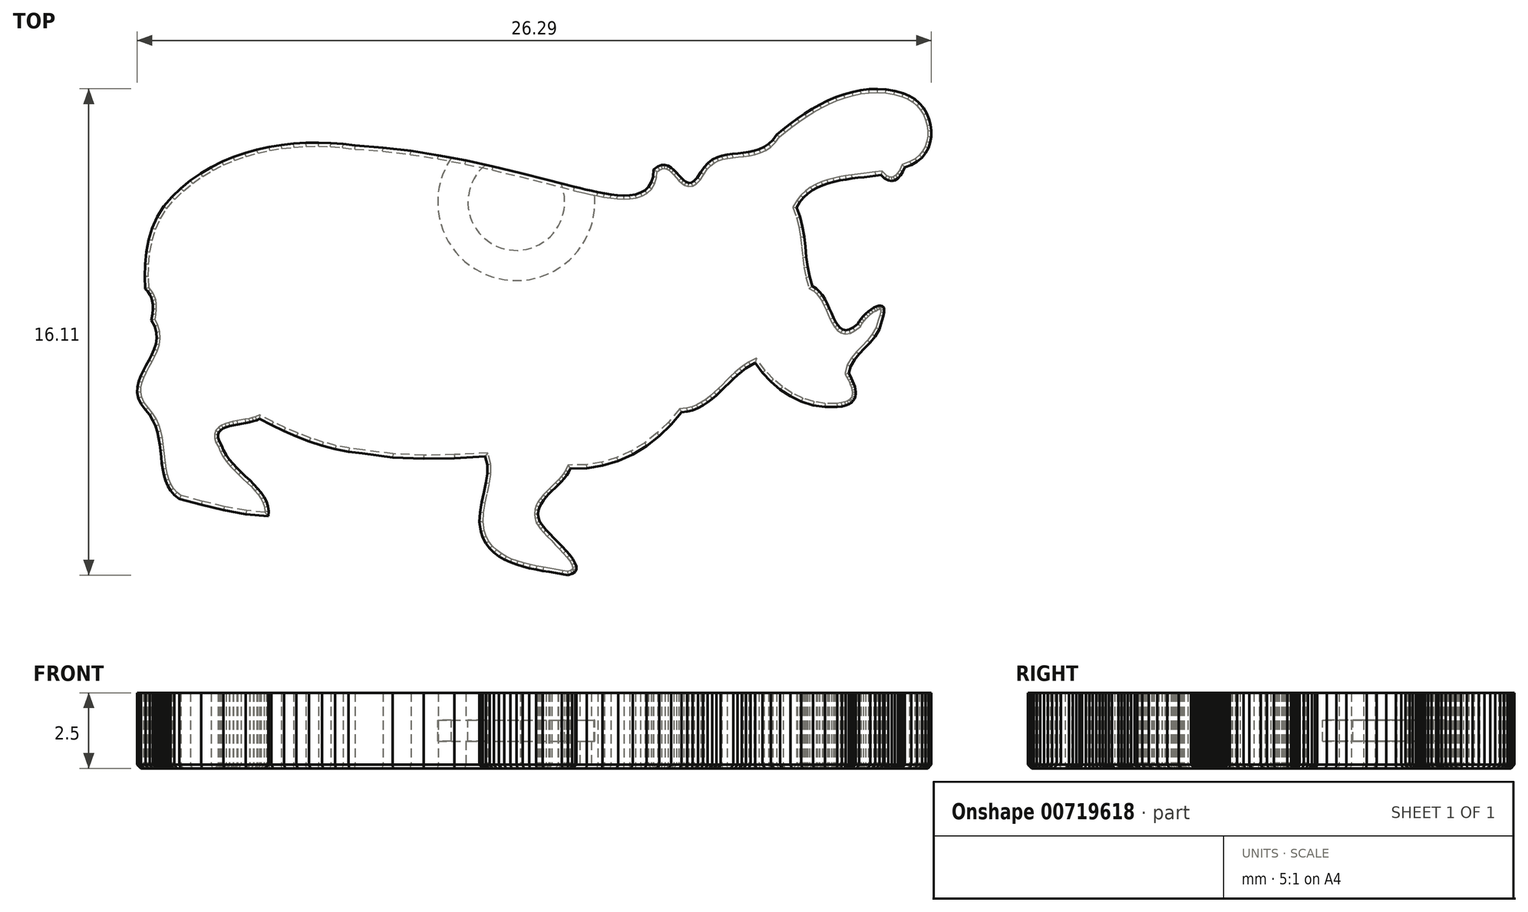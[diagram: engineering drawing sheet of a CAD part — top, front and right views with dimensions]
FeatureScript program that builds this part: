
annotation { "Feature Type Name" : "Feature", "Feature Type Description" : "" }
export const myFeature = defineFeature(function(context is Context, id is Id, definition is map)
    precondition{}
    {
        {
            var Q0;
            Q0=qCreatedBy(makeId("Top.planeOp"),FACE);
            var sketch = newSketch(context, id + "F0", { "sketchPlane" : qUnion([Q0])});
            skLineSegment(sketch, "E0", {"start": v(0.97, -8.24) * mm, "end": v(0.77, -8.2) * mm});
            skLineSegment(sketch, "E1", {"start": v(0.77, -8.2) * mm, "end": v(0.56, -8.17) * mm});
            skLineSegment(sketch, "E2", {"start": v(0.56, -8.17) * mm, "end": v(0.35, -8.14) * mm});
            skLineSegment(sketch, "E3", {"start": v(0.35, -8.14) * mm, "end": v(0.13, -8.1) * mm});
            skLineSegment(sketch, "E4", {"start": v(0.13, -8.1) * mm, "end": v(-0.09, -8.06) * mm});
            skLineSegment(sketch, "E5", {"start": v(-0.09, -8.06) * mm, "end": v(-0.3, -8.01) * mm});
            skLineSegment(sketch, "E6", {"start": v(-0.3, -8.01) * mm, "end": v(-0.52, -7.96) * mm});
            skLineSegment(sketch, "E7", {"start": v(-0.52, -7.96) * mm, "end": v(-0.73, -7.9) * mm});
            skLineSegment(sketch, "E8", {"start": v(-0.73, -7.9) * mm, "end": v(-0.94, -7.82) * mm});
            skLineSegment(sketch, "E9", {"start": v(-0.94, -7.82) * mm, "end": v(-1.13, -7.73) * mm});
            skLineSegment(sketch, "E10", {"start": v(-1.13, -7.73) * mm, "end": v(-1.3, -7.62) * mm});
            skLineSegment(sketch, "E11", {"start": v(-1.3, -7.62) * mm, "end": v(-1.47, -7.5) * mm});
            skLineSegment(sketch, "E12", {"start": v(-1.47, -7.5) * mm, "end": v(-1.62, -7.36) * mm});
            skLineSegment(sketch, "E13", {"start": v(-1.62, -7.36) * mm, "end": v(-1.74, -7.2) * mm});
            skLineSegment(sketch, "E14", {"start": v(-1.74, -7.2) * mm, "end": v(-1.84, -7) * mm});
            skLineSegment(sketch, "E15", {"start": v(-1.84, -7) * mm, "end": v(-1.92, -6.8) * mm});
            skLineSegment(sketch, "E16", {"start": v(-1.92, -6.8) * mm, "end": v(-1.96, -6.48) * mm});
            skLineSegment(sketch, "E17", {"start": v(-1.96, -6.48) * mm, "end": v(-1.94, -6.16) * mm});
            skLineSegment(sketch, "E18", {"start": v(-1.94, -6.16) * mm, "end": v(-1.89, -5.83) * mm});
            skLineSegment(sketch, "E19", {"start": v(-1.89, -5.83) * mm, "end": v(-1.81, -5.5) * mm});
            skLineSegment(sketch, "E20", {"start": v(-1.81, -5.5) * mm, "end": v(-1.74, -5.18) * mm});
            skLineSegment(sketch, "E21", {"start": v(-1.74, -5.18) * mm, "end": v(-1.7, -4.88) * mm});
            skLineSegment(sketch, "E22", {"start": v(-1.7, -4.88) * mm, "end": v(-1.7, -4.58) * mm});
            skLineSegment(sketch, "E23", {"start": v(-1.7, -4.58) * mm, "end": v(-1.77, -4.31) * mm});
            skLineSegment(sketch, "E24", {"start": v(-1.77, -4.31) * mm, "end": v(-2.79, -4.37) * mm});
            skLineSegment(sketch, "E25", {"start": v(-2.79, -4.37) * mm, "end": v(-3.8, -4.39) * mm});
            skLineSegment(sketch, "E26", {"start": v(-3.8, -4.39) * mm, "end": v(-4.83, -4.34) * mm});
            skLineSegment(sketch, "E27", {"start": v(-4.83, -4.34) * mm, "end": v(-5.84, -4.2) * mm});
            skLineSegment(sketch, "E28", {"start": v(-5.84, -4.2) * mm, "end": v(-6.3, -4.15) * mm});
            skLineSegment(sketch, "E29", {"start": v(-6.3, -4.15) * mm, "end": v(-6.73, -4.06) * mm});
            skLineSegment(sketch, "E30", {"start": v(-6.73, -4.06) * mm, "end": v(-7.17, -3.95) * mm});
            skLineSegment(sketch, "E31", {"start": v(-7.17, -3.95) * mm, "end": v(-7.6, -3.8) * mm});
            skLineSegment(sketch, "E32", {"start": v(-7.6, -3.8) * mm, "end": v(-8.02, -3.64) * mm});
            skLineSegment(sketch, "E33", {"start": v(-8.02, -3.64) * mm, "end": v(-8.43, -3.46) * mm});
            skLineSegment(sketch, "E34", {"start": v(-8.43, -3.46) * mm, "end": v(-8.84, -3.27) * mm});
            skLineSegment(sketch, "E35", {"start": v(-8.84, -3.27) * mm, "end": v(-9.24, -3.07) * mm});
            skLineSegment(sketch, "E36", {"start": v(-9.24, -3.07) * mm, "end": v(-9.33, -3.1) * mm});
            skLineSegment(sketch, "E37", {"start": v(-9.33, -3.1) * mm, "end": v(-9.44, -3.14) * mm});
            skLineSegment(sketch, "E38", {"start": v(-9.44, -3.14) * mm, "end": v(-9.56, -3.17) * mm});
            skLineSegment(sketch, "E39", {"start": v(-9.56, -3.17) * mm, "end": v(-9.7, -3.2) * mm});
            skLineSegment(sketch, "E40", {"start": v(-9.7, -3.2) * mm, "end": v(-9.83, -3.22) * mm});
            skLineSegment(sketch, "E41", {"start": v(-9.83, -3.22) * mm, "end": v(-9.97, -3.25) * mm});
            skLineSegment(sketch, "E42", {"start": v(-9.97, -3.25) * mm, "end": v(-10.1, -3.27) * mm});
            skLineSegment(sketch, "E43", {"start": v(-10.1, -3.27) * mm, "end": v(-10.23, -3.3) * mm});
            skLineSegment(sketch, "E44", {"start": v(-10.23, -3.3) * mm, "end": v(-10.34, -3.34) * mm});
            skLineSegment(sketch, "E45", {"start": v(-10.34, -3.34) * mm, "end": v(-10.44, -3.39) * mm});
            skLineSegment(sketch, "E46", {"start": v(-10.44, -3.39) * mm, "end": v(-10.52, -3.44) * mm});
            skLineSegment(sketch, "E47", {"start": v(-10.52, -3.44) * mm, "end": v(-10.58, -3.5) * mm});
            skLineSegment(sketch, "E48", {"start": v(-10.58, -3.5) * mm, "end": v(-10.6, -3.59) * mm});
            skLineSegment(sketch, "E49", {"start": v(-10.6, -3.59) * mm, "end": v(-10.6, -3.69) * mm});
            skLineSegment(sketch, "E50", {"start": v(-10.6, -3.69) * mm, "end": v(-10.57, -3.8) * mm});
            skLineSegment(sketch, "E51", {"start": v(-10.57, -3.8) * mm, "end": v(-10.5, -3.94) * mm});
            skLineSegment(sketch, "E52", {"start": v(-10.5, -3.94) * mm, "end": v(-10.43, -4.1) * mm});
            skLineSegment(sketch, "E53", {"start": v(-10.43, -4.1) * mm, "end": v(-10.34, -4.26) * mm});
            skLineSegment(sketch, "E54", {"start": v(-10.34, -4.26) * mm, "end": v(-10.24, -4.4) * mm});
            skLineSegment(sketch, "E55", {"start": v(-10.24, -4.4) * mm, "end": v(-10.12, -4.55) * mm});
            skLineSegment(sketch, "E56", {"start": v(-10.12, -4.55) * mm, "end": v(-9.98, -4.7) * mm});
            skLineSegment(sketch, "E57", {"start": v(-9.98, -4.7) * mm, "end": v(-9.84, -4.83) * mm});
            skLineSegment(sketch, "E58", {"start": v(-9.84, -4.83) * mm, "end": v(-9.7, -4.96) * mm});
            skLineSegment(sketch, "E59", {"start": v(-9.7, -4.96) * mm, "end": v(-9.56, -5.1) * mm});
            skLineSegment(sketch, "E60", {"start": v(-9.56, -5.1) * mm, "end": v(-9.43, -5.23) * mm});
            skLineSegment(sketch, "E61", {"start": v(-9.43, -5.23) * mm, "end": v(-9.3, -5.37) * mm});
            skLineSegment(sketch, "E62", {"start": v(-9.3, -5.37) * mm, "end": v(-9.18, -5.5) * mm});
            skLineSegment(sketch, "E63", {"start": v(-9.18, -5.5) * mm, "end": v(-9.09, -5.65) * mm});
            skLineSegment(sketch, "E64", {"start": v(-9.09, -5.65) * mm, "end": v(-9, -5.8) * mm});
            skLineSegment(sketch, "E65", {"start": v(-9, -5.8) * mm, "end": v(-8.96, -5.95) * mm});
            skLineSegment(sketch, "E66", {"start": v(-8.96, -5.95) * mm, "end": v(-8.94, -6.12) * mm});
            skLineSegment(sketch, "E67", {"start": v(-8.94, -6.12) * mm, "end": v(-8.95, -6.3) * mm});
            skLineSegment(sketch, "E68", {"start": v(-8.95, -6.3) * mm, "end": v(-9.7, -6.22) * mm});
            skLineSegment(sketch, "E69", {"start": v(-9.7, -6.22) * mm, "end": v(-10.43, -6.08) * mm});
            skLineSegment(sketch, "E70", {"start": v(-10.43, -6.08) * mm, "end": v(-11.17, -5.9) * mm});
            skLineSegment(sketch, "E71", {"start": v(-11.17, -5.9) * mm, "end": v(-11.9, -5.71) * mm});
            skLineSegment(sketch, "E72", {"start": v(-11.9, -5.71) * mm, "end": v(-12.05, -5.58) * mm});
            skLineSegment(sketch, "E73", {"start": v(-12.05, -5.58) * mm, "end": v(-12.18, -5.44) * mm});
            skLineSegment(sketch, "E74", {"start": v(-12.18, -5.44) * mm, "end": v(-12.28, -5.28) * mm});
            skLineSegment(sketch, "E75", {"start": v(-12.28, -5.28) * mm, "end": v(-12.35, -5.11) * mm});
            skLineSegment(sketch, "E76", {"start": v(-12.35, -5.11) * mm, "end": v(-12.4, -4.93) * mm});
            skLineSegment(sketch, "E77", {"start": v(-12.4, -4.93) * mm, "end": v(-12.44, -4.73) * mm});
            skLineSegment(sketch, "E78", {"start": v(-12.44, -4.73) * mm, "end": v(-12.47, -4.53) * mm});
            skLineSegment(sketch, "E79", {"start": v(-12.47, -4.53) * mm, "end": v(-12.5, -4.33) * mm});
            skLineSegment(sketch, "E80", {"start": v(-12.5, -4.33) * mm, "end": v(-12.52, -4.12) * mm});
            skLineSegment(sketch, "E81", {"start": v(-12.52, -4.12) * mm, "end": v(-12.54, -3.91) * mm});
            skLineSegment(sketch, "E82", {"start": v(-12.54, -3.91) * mm, "end": v(-12.57, -3.7) * mm});
            skLineSegment(sketch, "E83", {"start": v(-12.57, -3.7) * mm, "end": v(-12.62, -3.5) * mm});
            skLineSegment(sketch, "E84", {"start": v(-12.62, -3.5) * mm, "end": v(-12.68, -3.3) * mm});
            skLineSegment(sketch, "E85", {"start": v(-12.68, -3.3) * mm, "end": v(-12.76, -3.12) * mm});
            skLineSegment(sketch, "E86", {"start": v(-12.76, -3.12) * mm, "end": v(-12.87, -2.94) * mm});
            skLineSegment(sketch, "E87", {"start": v(-12.87, -2.94) * mm, "end": v(-13.01, -2.77) * mm});
            skLineSegment(sketch, "E88", {"start": v(-13.01, -2.77) * mm, "end": v(-13.16, -2.57) * mm});
            skLineSegment(sketch, "E89", {"start": v(-13.16, -2.57) * mm, "end": v(-13.25, -2.38) * mm});
            skLineSegment(sketch, "E90", {"start": v(-13.25, -2.38) * mm, "end": v(-13.29, -2.19) * mm});
            skLineSegment(sketch, "E91", {"start": v(-13.29, -2.19) * mm, "end": v(-13.28, -2) * mm});
            skLineSegment(sketch, "E92", {"start": v(-13.28, -2) * mm, "end": v(-13.24, -1.82) * mm});
            skLineSegment(sketch, "E93", {"start": v(-13.24, -1.82) * mm, "end": v(-13.18, -1.65) * mm});
            skLineSegment(sketch, "E94", {"start": v(-13.18, -1.65) * mm, "end": v(-13.1, -1.47) * mm});
            skLineSegment(sketch, "E95", {"start": v(-13.1, -1.47) * mm, "end": v(-13, -1.3) * mm});
            skLineSegment(sketch, "E96", {"start": v(-13, -1.3) * mm, "end": v(-12.9, -1.12) * mm});
            skLineSegment(sketch, "E97", {"start": v(-12.9, -1.12) * mm, "end": v(-12.8, -0.94) * mm});
            skLineSegment(sketch, "E98", {"start": v(-12.8, -0.94) * mm, "end": v(-12.73, -0.76) * mm});
            skLineSegment(sketch, "E99", {"start": v(-12.73, -0.76) * mm, "end": v(-12.67, -0.58) * mm});
            skLineSegment(sketch, "E100", {"start": v(-12.67, -0.58) * mm, "end": v(-12.65, -0.4) * mm});
            skLineSegment(sketch, "E101", {"start": v(-12.65, -0.4) * mm, "end": v(-12.66, -0.2) * mm});
            skLineSegment(sketch, "E102", {"start": v(-12.66, -0.2) * mm, "end": v(-12.71, 0) * mm});
            skLineSegment(sketch, "E103", {"start": v(-12.71, 0) * mm, "end": v(-12.82, 0.2) * mm});
            skLineSegment(sketch, "E104", {"start": v(-12.82, 0.2) * mm, "end": v(-12.79, 0.4) * mm});
            skLineSegment(sketch, "E105", {"start": v(-12.79, 0.4) * mm, "end": v(-12.77, 0.58) * mm});
            skLineSegment(sketch, "E106", {"start": v(-12.77, 0.58) * mm, "end": v(-12.77, 0.72) * mm});
            skLineSegment(sketch, "E107", {"start": v(-12.77, 0.72) * mm, "end": v(-12.79, 0.85) * mm});
            skLineSegment(sketch, "E108", {"start": v(-12.79, 0.85) * mm, "end": v(-12.82, 0.96) * mm});
            skLineSegment(sketch, "E109", {"start": v(-12.82, 0.96) * mm, "end": v(-12.87, 1.06) * mm});
            skLineSegment(sketch, "E110", {"start": v(-12.87, 1.06) * mm, "end": v(-12.94, 1.15) * mm});
            skLineSegment(sketch, "E111", {"start": v(-12.94, 1.15) * mm, "end": v(-13.02, 1.24) * mm});
            skLineSegment(sketch, "E112", {"start": v(-13.02, 1.24) * mm, "end": v(-13.04, 1.65) * mm});
            skLineSegment(sketch, "E113", {"start": v(-13.04, 1.65) * mm, "end": v(-13.03, 2.06) * mm});
            skLineSegment(sketch, "E114", {"start": v(-13.03, 2.06) * mm, "end": v(-12.99, 2.47) * mm});
            skLineSegment(sketch, "E115", {"start": v(-12.99, 2.47) * mm, "end": v(-12.9, 2.87) * mm});
            skLineSegment(sketch, "E116", {"start": v(-12.9, 2.87) * mm, "end": v(-12.8, 3.25) * mm});
            skLineSegment(sketch, "E117", {"start": v(-12.8, 3.25) * mm, "end": v(-12.63, 3.62) * mm});
            skLineSegment(sketch, "E118", {"start": v(-12.63, 3.62) * mm, "end": v(-12.4, 3.97) * mm});
            skLineSegment(sketch, "E119", {"start": v(-12.4, 3.97) * mm, "end": v(-12.14, 4.29) * mm});
            skLineSegment(sketch, "E120", {"start": v(-12.14, 4.29) * mm, "end": v(-11.84, 4.58) * mm});
            skLineSegment(sketch, "E121", {"start": v(-11.84, 4.58) * mm, "end": v(-11.52, 4.83) * mm});
            skLineSegment(sketch, "E122", {"start": v(-11.52, 4.83) * mm, "end": v(-11.19, 5.07) * mm});
            skLineSegment(sketch, "E123", {"start": v(-11.19, 5.07) * mm, "end": v(-10.84, 5.27) * mm});
            skLineSegment(sketch, "E124", {"start": v(-10.84, 5.27) * mm, "end": v(-10.48, 5.45) * mm});
            skLineSegment(sketch, "E125", {"start": v(-10.48, 5.45) * mm, "end": v(-10.1, 5.61) * mm});
            skLineSegment(sketch, "E126", {"start": v(-10.1, 5.61) * mm, "end": v(-9.72, 5.74) * mm});
            skLineSegment(sketch, "E127", {"start": v(-9.72, 5.74) * mm, "end": v(-9.32, 5.85) * mm});
            skLineSegment(sketch, "E128", {"start": v(-9.32, 5.85) * mm, "end": v(-8.92, 5.94) * mm});
            skLineSegment(sketch, "E129", {"start": v(-8.92, 5.94) * mm, "end": v(-8.52, 6) * mm});
            skLineSegment(sketch, "E130", {"start": v(-8.52, 6) * mm, "end": v(-8.1, 6.05) * mm});
            skLineSegment(sketch, "E131", {"start": v(-8.1, 6.05) * mm, "end": v(-7.7, 6.08) * mm});
            skLineSegment(sketch, "E132", {"start": v(-7.7, 6.08) * mm, "end": v(-7.29, 6.08) * mm});
            skLineSegment(sketch, "E133", {"start": v(-7.29, 6.08) * mm, "end": v(-6.88, 6.07) * mm});
            skLineSegment(sketch, "E134", {"start": v(-6.88, 6.07) * mm, "end": v(-6.47, 6.04) * mm});
            skLineSegment(sketch, "E135", {"start": v(-6.47, 6.04) * mm, "end": v(-6.07, 6) * mm});
            skLineSegment(sketch, "E136", {"start": v(-6.07, 6) * mm, "end": v(-5.15, 5.92) * mm});
            skLineSegment(sketch, "E137", {"start": v(-5.15, 5.92) * mm, "end": v(-4.23, 5.81) * mm});
            skLineSegment(sketch, "E138", {"start": v(-4.23, 5.81) * mm, "end": v(-3.31, 5.67) * mm});
            skLineSegment(sketch, "E139", {"start": v(-3.31, 5.67) * mm, "end": v(-2.4, 5.5) * mm});
            skLineSegment(sketch, "E140", {"start": v(-2.4, 5.5) * mm, "end": v(-1.5, 5.3) * mm});
            skLineSegment(sketch, "E141", {"start": v(-1.5, 5.3) * mm, "end": v(-0.6, 5.08) * mm});
            skLineSegment(sketch, "E142", {"start": v(-0.6, 5.08) * mm, "end": v(0.3, 4.85) * mm});
            skLineSegment(sketch, "E143", {"start": v(0.3, 4.85) * mm, "end": v(1.2, 4.62) * mm});
            skLineSegment(sketch, "E144", {"start": v(1.2, 4.62) * mm, "end": v(1.36, 4.58) * mm});
            skLineSegment(sketch, "E145", {"start": v(1.36, 4.58) * mm, "end": v(1.55, 4.53) * mm});
            skLineSegment(sketch, "E146", {"start": v(1.55, 4.53) * mm, "end": v(1.75, 4.49) * mm});
            skLineSegment(sketch, "E147", {"start": v(1.75, 4.49) * mm, "end": v(1.96, 4.44) * mm});
            skLineSegment(sketch, "E148", {"start": v(1.96, 4.44) * mm, "end": v(2.18, 4.4) * mm});
            skLineSegment(sketch, "E149", {"start": v(2.18, 4.4) * mm, "end": v(2.4, 4.37) * mm});
            skLineSegment(sketch, "E150", {"start": v(2.4, 4.37) * mm, "end": v(2.61, 4.34) * mm});
            skLineSegment(sketch, "E151", {"start": v(2.61, 4.34) * mm, "end": v(2.82, 4.33) * mm});
            skLineSegment(sketch, "E152", {"start": v(2.82, 4.33) * mm, "end": v(3.02, 4.34) * mm});
            skLineSegment(sketch, "E153", {"start": v(3.02, 4.34) * mm, "end": v(3.2, 4.37) * mm});
            skLineSegment(sketch, "E154", {"start": v(3.2, 4.37) * mm, "end": v(3.38, 4.42) * mm});
            skLineSegment(sketch, "E155", {"start": v(3.38, 4.42) * mm, "end": v(3.52, 4.5) * mm});
            skLineSegment(sketch, "E156", {"start": v(3.52, 4.5) * mm, "end": v(3.64, 4.62) * mm});
            skLineSegment(sketch, "E157", {"start": v(3.64, 4.62) * mm, "end": v(3.73, 4.77) * mm});
            skLineSegment(sketch, "E158", {"start": v(3.73, 4.77) * mm, "end": v(3.79, 4.96) * mm});
            skLineSegment(sketch, "E159", {"start": v(3.79, 4.96) * mm, "end": v(3.8, 5.19) * mm});
            skLineSegment(sketch, "E160", {"start": v(3.8, 5.19) * mm, "end": v(3.94, 5.29) * mm});
            skLineSegment(sketch, "E161", {"start": v(3.94, 5.29) * mm, "end": v(4.07, 5.34) * mm});
            skLineSegment(sketch, "E162", {"start": v(4.07, 5.34) * mm, "end": v(4.19, 5.35) * mm});
            skLineSegment(sketch, "E163", {"start": v(4.19, 5.35) * mm, "end": v(4.3, 5.32) * mm});
            skLineSegment(sketch, "E164", {"start": v(4.3, 5.32) * mm, "end": v(4.4, 5.26) * mm});
            skLineSegment(sketch, "E165", {"start": v(4.4, 5.26) * mm, "end": v(4.48, 5.18) * mm});
            skLineSegment(sketch, "E166", {"start": v(4.48, 5.18) * mm, "end": v(4.57, 5.1) * mm});
            skLineSegment(sketch, "E167", {"start": v(4.57, 5.1) * mm, "end": v(4.65, 5) * mm});
            skLineSegment(sketch, "E168", {"start": v(4.65, 5) * mm, "end": v(4.73, 4.91) * mm});
            skLineSegment(sketch, "E169", {"start": v(4.73, 4.91) * mm, "end": v(4.8, 4.84) * mm});
            skLineSegment(sketch, "E170", {"start": v(4.8, 4.84) * mm, "end": v(4.89, 4.78) * mm});
            skLineSegment(sketch, "E171", {"start": v(4.89, 4.78) * mm, "end": v(4.97, 4.75) * mm});
            skLineSegment(sketch, "E172", {"start": v(4.97, 4.75) * mm, "end": v(5.06, 4.76) * mm});
            skLineSegment(sketch, "E173", {"start": v(5.06, 4.76) * mm, "end": v(5.15, 4.82) * mm});
            skLineSegment(sketch, "E174", {"start": v(5.15, 4.82) * mm, "end": v(5.26, 4.93) * mm});
            skLineSegment(sketch, "E175", {"start": v(5.26, 4.93) * mm, "end": v(5.37, 5.1) * mm});
            skLineSegment(sketch, "E176", {"start": v(5.37, 5.1) * mm, "end": v(5.48, 5.28) * mm});
            skLineSegment(sketch, "E177", {"start": v(5.48, 5.28) * mm, "end": v(5.61, 5.41) * mm});
            skLineSegment(sketch, "E178", {"start": v(5.61, 5.41) * mm, "end": v(5.75, 5.52) * mm});
            skLineSegment(sketch, "E179", {"start": v(5.75, 5.52) * mm, "end": v(5.9, 5.6) * mm});
            skLineSegment(sketch, "E180", {"start": v(5.9, 5.6) * mm, "end": v(6.07, 5.65) * mm});
            skLineSegment(sketch, "E181", {"start": v(6.07, 5.65) * mm, "end": v(6.24, 5.68) * mm});
            skLineSegment(sketch, "E182", {"start": v(6.24, 5.68) * mm, "end": v(6.42, 5.7) * mm});
            skLineSegment(sketch, "E183", {"start": v(6.42, 5.7) * mm, "end": v(6.6, 5.73) * mm});
            skLineSegment(sketch, "E184", {"start": v(6.6, 5.73) * mm, "end": v(6.77, 5.75) * mm});
            skLineSegment(sketch, "E185", {"start": v(6.77, 5.75) * mm, "end": v(6.95, 5.77) * mm});
            skLineSegment(sketch, "E186", {"start": v(6.95, 5.77) * mm, "end": v(7.13, 5.8) * mm});
            skLineSegment(sketch, "E187", {"start": v(7.13, 5.8) * mm, "end": v(7.3, 5.86) * mm});
            skLineSegment(sketch, "E188", {"start": v(7.3, 5.86) * mm, "end": v(7.46, 5.94) * mm});
            skLineSegment(sketch, "E189", {"start": v(7.46, 5.94) * mm, "end": v(7.62, 6.04) * mm});
            skLineSegment(sketch, "E190", {"start": v(7.62, 6.04) * mm, "end": v(7.76, 6.18) * mm});
            skLineSegment(sketch, "E191", {"start": v(7.76, 6.18) * mm, "end": v(7.89, 6.35) * mm});
            skLineSegment(sketch, "E192", {"start": v(7.89, 6.35) * mm, "end": v(8.1, 6.53) * mm});
            skLineSegment(sketch, "E193", {"start": v(8.1, 6.53) * mm, "end": v(8.33, 6.7) * mm});
            skLineSegment(sketch, "E194", {"start": v(8.33, 6.7) * mm, "end": v(8.56, 6.88) * mm});
            skLineSegment(sketch, "E195", {"start": v(8.56, 6.88) * mm, "end": v(8.8, 7.04) * mm});
            skLineSegment(sketch, "E196", {"start": v(8.8, 7.04) * mm, "end": v(9.05, 7.2) * mm});
            skLineSegment(sketch, "E197", {"start": v(9.05, 7.2) * mm, "end": v(9.3, 7.34) * mm});
            skLineSegment(sketch, "E198", {"start": v(9.3, 7.34) * mm, "end": v(9.57, 7.47) * mm});
            skLineSegment(sketch, "E199", {"start": v(9.57, 7.47) * mm, "end": v(9.83, 7.59) * mm});
            skLineSegment(sketch, "E200", {"start": v(9.83, 7.59) * mm, "end": v(10.1, 7.69) * mm});
            skLineSegment(sketch, "E201", {"start": v(10.1, 7.69) * mm, "end": v(10.38, 7.76) * mm});
            skLineSegment(sketch, "E202", {"start": v(10.38, 7.76) * mm, "end": v(10.66, 7.82) * mm});
            skLineSegment(sketch, "E203", {"start": v(10.66, 7.82) * mm, "end": v(10.94, 7.86) * mm});
            skLineSegment(sketch, "E204", {"start": v(10.94, 7.86) * mm, "end": v(11.22, 7.87) * mm});
            skLineSegment(sketch, "E205", {"start": v(11.22, 7.87) * mm, "end": v(11.5, 7.85) * mm});
            skLineSegment(sketch, "E206", {"start": v(11.5, 7.85) * mm, "end": v(11.8, 7.8) * mm});
            skLineSegment(sketch, "E207", {"start": v(11.8, 7.8) * mm, "end": v(12.07, 7.72) * mm});
            skLineSegment(sketch, "E208", {"start": v(12.07, 7.72) * mm, "end": v(12.28, 7.64) * mm});
            skLineSegment(sketch, "E209", {"start": v(12.28, 7.64) * mm, "end": v(12.46, 7.53) * mm});
            skLineSegment(sketch, "E210", {"start": v(12.46, 7.53) * mm, "end": v(12.61, 7.39) * mm});
            skLineSegment(sketch, "E211", {"start": v(12.61, 7.39) * mm, "end": v(12.74, 7.23) * mm});
            skLineSegment(sketch, "E212", {"start": v(12.74, 7.23) * mm, "end": v(12.85, 7.06) * mm});
            skLineSegment(sketch, "E213", {"start": v(12.85, 7.06) * mm, "end": v(12.93, 6.87) * mm});
            skLineSegment(sketch, "E214", {"start": v(12.93, 6.87) * mm, "end": v(12.98, 6.68) * mm});
            skLineSegment(sketch, "E215", {"start": v(12.98, 6.68) * mm, "end": v(13, 6.48) * mm});
            skLineSegment(sketch, "E216", {"start": v(13, 6.48) * mm, "end": v(13, 6.29) * mm});
            skLineSegment(sketch, "E217", {"start": v(13, 6.29) * mm, "end": v(12.97, 6.1) * mm});
            skLineSegment(sketch, "E218", {"start": v(12.97, 6.1) * mm, "end": v(12.9, 5.91) * mm});
            skLineSegment(sketch, "E219", {"start": v(12.9, 5.91) * mm, "end": v(12.81, 5.74) * mm});
            skLineSegment(sketch, "E220", {"start": v(12.81, 5.74) * mm, "end": v(12.69, 5.59) * mm});
            skLineSegment(sketch, "E221", {"start": v(12.69, 5.59) * mm, "end": v(12.53, 5.45) * mm});
            skLineSegment(sketch, "E222", {"start": v(12.53, 5.45) * mm, "end": v(12.34, 5.35) * mm});
            skLineSegment(sketch, "E223", {"start": v(12.34, 5.35) * mm, "end": v(12.12, 5.27) * mm});
            skLineSegment(sketch, "E224", {"start": v(12.12, 5.27) * mm, "end": v(12.06, 5.12) * mm});
            skLineSegment(sketch, "E225", {"start": v(12.06, 5.12) * mm, "end": v(11.98, 5) * mm});
            skLineSegment(sketch, "E226", {"start": v(11.98, 5) * mm, "end": v(11.9, 4.9) * mm});
            skLineSegment(sketch, "E227", {"start": v(11.9, 4.9) * mm, "end": v(11.8, 4.84) * mm});
            skLineSegment(sketch, "E228", {"start": v(11.8, 4.84) * mm, "end": v(11.69, 4.81) * mm});
            skLineSegment(sketch, "E229", {"start": v(11.69, 4.81) * mm, "end": v(11.57, 4.83) * mm});
            skLineSegment(sketch, "E230", {"start": v(11.57, 4.83) * mm, "end": v(11.45, 4.9) * mm});
            skLineSegment(sketch, "E231", {"start": v(11.45, 4.9) * mm, "end": v(11.33, 5.02) * mm});
            skLineSegment(sketch, "E232", {"start": v(11.33, 5.02) * mm, "end": v(11.16, 5) * mm});
            skLineSegment(sketch, "E233", {"start": v(11.16, 5) * mm, "end": v(10.97, 4.97) * mm});
            skLineSegment(sketch, "E234", {"start": v(10.97, 4.97) * mm, "end": v(10.77, 4.94) * mm});
            skLineSegment(sketch, "E235", {"start": v(10.77, 4.94) * mm, "end": v(10.58, 4.92) * mm});
            skLineSegment(sketch, "E236", {"start": v(10.58, 4.92) * mm, "end": v(10.38, 4.9) * mm});
            skLineSegment(sketch, "E237", {"start": v(10.38, 4.9) * mm, "end": v(10.17, 4.87) * mm});
            skLineSegment(sketch, "E238", {"start": v(10.17, 4.87) * mm, "end": v(9.97, 4.83) * mm});
            skLineSegment(sketch, "E239", {"start": v(9.97, 4.83) * mm, "end": v(9.78, 4.79) * mm});
            skLineSegment(sketch, "E240", {"start": v(9.78, 4.79) * mm, "end": v(9.58, 4.74) * mm});
            skLineSegment(sketch, "E241", {"start": v(9.58, 4.74) * mm, "end": v(9.4, 4.67) * mm});
            skLineSegment(sketch, "E242", {"start": v(9.4, 4.67) * mm, "end": v(9.22, 4.6) * mm});
            skLineSegment(sketch, "E243", {"start": v(9.22, 4.6) * mm, "end": v(9.06, 4.5) * mm});
            skLineSegment(sketch, "E244", {"start": v(9.06, 4.5) * mm, "end": v(8.9, 4.4) * mm});
            skLineSegment(sketch, "E245", {"start": v(8.9, 4.4) * mm, "end": v(8.77, 4.26) * mm});
            skLineSegment(sketch, "E246", {"start": v(8.77, 4.26) * mm, "end": v(8.65, 4.11) * mm});
            skLineSegment(sketch, "E247", {"start": v(8.65, 4.11) * mm, "end": v(8.55, 3.94) * mm});
            skLineSegment(sketch, "E248", {"start": v(8.55, 3.94) * mm, "end": v(8.66, 3.62) * mm});
            skLineSegment(sketch, "E249", {"start": v(8.66, 3.62) * mm, "end": v(8.74, 3.3) * mm});
            skLineSegment(sketch, "E250", {"start": v(8.74, 3.3) * mm, "end": v(8.79, 2.97) * mm});
            skLineSegment(sketch, "E251", {"start": v(8.79, 2.97) * mm, "end": v(8.83, 2.64) * mm});
            skLineSegment(sketch, "E252", {"start": v(8.83, 2.64) * mm, "end": v(8.86, 2.3) * mm});
            skLineSegment(sketch, "E253", {"start": v(8.86, 2.3) * mm, "end": v(8.9, 1.97) * mm});
            skLineSegment(sketch, "E254", {"start": v(8.9, 1.97) * mm, "end": v(8.97, 1.65) * mm});
            skLineSegment(sketch, "E255", {"start": v(8.97, 1.65) * mm, "end": v(9.06, 1.33) * mm});
            skLineSegment(sketch, "E256", {"start": v(9.06, 1.33) * mm, "end": v(9.18, 1.26) * mm});
            skLineSegment(sketch, "E257", {"start": v(9.18, 1.26) * mm, "end": v(9.3, 1.16) * mm});
            skLineSegment(sketch, "E258", {"start": v(9.3, 1.16) * mm, "end": v(9.4, 1.04) * mm});
            skLineSegment(sketch, "E259", {"start": v(9.4, 1.04) * mm, "end": v(9.48, 0.9) * mm});
            skLineSegment(sketch, "E260", {"start": v(9.48, 0.9) * mm, "end": v(9.56, 0.75) * mm});
            skLineSegment(sketch, "E261", {"start": v(9.56, 0.75) * mm, "end": v(9.63, 0.6) * mm});
            skLineSegment(sketch, "E262", {"start": v(9.63, 0.6) * mm, "end": v(9.7, 0.44) * mm});
            skLineSegment(sketch, "E263", {"start": v(9.7, 0.44) * mm, "end": v(9.76, 0.3) * mm});
            skLineSegment(sketch, "E264", {"start": v(9.76, 0.3) * mm, "end": v(9.82, 0.16) * mm});
            skLineSegment(sketch, "E265", {"start": v(9.82, 0.16) * mm, "end": v(9.9, 0.05) * mm});
            skLineSegment(sketch, "E266", {"start": v(9.9, 0.05) * mm, "end": v(9.97, -0.04) * mm});
            skLineSegment(sketch, "E267", {"start": v(9.97, -0.04) * mm, "end": v(10.06, -0.1) * mm});
            skLineSegment(sketch, "E268", {"start": v(10.06, -0.1) * mm, "end": v(10.16, -0.13) * mm});
            skLineSegment(sketch, "E269", {"start": v(10.16, -0.13) * mm, "end": v(10.28, -0.1) * mm});
            skLineSegment(sketch, "E270", {"start": v(10.28, -0.1) * mm, "end": v(10.41, -0.04) * mm});
            skLineSegment(sketch, "E271", {"start": v(10.41, -0.04) * mm, "end": v(10.57, 0.08) * mm});
            skLineSegment(sketch, "E272", {"start": v(10.57, 0.08) * mm, "end": v(10.61, 0.16) * mm});
            skLineSegment(sketch, "E273", {"start": v(10.61, 0.16) * mm, "end": v(10.68, 0.25) * mm});
            skLineSegment(sketch, "E274", {"start": v(10.68, 0.25) * mm, "end": v(10.75, 0.34) * mm});
            skLineSegment(sketch, "E275", {"start": v(10.75, 0.34) * mm, "end": v(10.83, 0.42) * mm});
            skLineSegment(sketch, "E276", {"start": v(10.83, 0.42) * mm, "end": v(10.92, 0.5) * mm});
            skLineSegment(sketch, "E277", {"start": v(10.92, 0.5) * mm, "end": v(11, 0.56) * mm});
            skLineSegment(sketch, "E278", {"start": v(11, 0.56) * mm, "end": v(11.1, 0.62) * mm});
            skLineSegment(sketch, "E279", {"start": v(11.1, 0.62) * mm, "end": v(11.18, 0.66) * mm});
            skLineSegment(sketch, "E280", {"start": v(11.18, 0.66) * mm, "end": v(11.26, 0.68) * mm});
            skLineSegment(sketch, "E281", {"start": v(11.26, 0.68) * mm, "end": v(11.32, 0.69) * mm});
            skLineSegment(sketch, "E282", {"start": v(11.32, 0.69) * mm, "end": v(11.38, 0.67) * mm});
            skLineSegment(sketch, "E283", {"start": v(11.38, 0.67) * mm, "end": v(11.42, 0.63) * mm});
            skLineSegment(sketch, "E284", {"start": v(11.42, 0.63) * mm, "end": v(11.44, 0.57) * mm});
            skLineSegment(sketch, "E285", {"start": v(11.44, 0.57) * mm, "end": v(11.44, 0.47) * mm});
            skLineSegment(sketch, "E286", {"start": v(11.44, 0.47) * mm, "end": v(11.42, 0.34) * mm});
            skLineSegment(sketch, "E287", {"start": v(11.42, 0.34) * mm, "end": v(11.37, 0.18) * mm});
            skLineSegment(sketch, "E288", {"start": v(11.37, 0.18) * mm, "end": v(11.28, -0.1) * mm});
            skLineSegment(sketch, "E289", {"start": v(11.28, -0.1) * mm, "end": v(11.15, -0.33) * mm});
            skLineSegment(sketch, "E290", {"start": v(11.15, -0.33) * mm, "end": v(10.98, -0.54) * mm});
            skLineSegment(sketch, "E291", {"start": v(10.98, -0.54) * mm, "end": v(10.8, -0.73) * mm});
            skLineSegment(sketch, "E292", {"start": v(10.8, -0.73) * mm, "end": v(10.62, -0.92) * mm});
            skLineSegment(sketch, "E293", {"start": v(10.62, -0.92) * mm, "end": v(10.46, -1.1) * mm});
            skLineSegment(sketch, "E294", {"start": v(10.46, -1.1) * mm, "end": v(10.34, -1.32) * mm});
            skLineSegment(sketch, "E295", {"start": v(10.34, -1.32) * mm, "end": v(10.27, -1.56) * mm});
            skLineSegment(sketch, "E296", {"start": v(10.27, -1.56) * mm, "end": v(10.32, -1.64) * mm});
            skLineSegment(sketch, "E297", {"start": v(10.32, -1.64) * mm, "end": v(10.36, -1.73) * mm});
            skLineSegment(sketch, "E298", {"start": v(10.36, -1.73) * mm, "end": v(10.4, -1.81) * mm});
            skLineSegment(sketch, "E299", {"start": v(10.4, -1.81) * mm, "end": v(10.44, -1.9) * mm});
            skLineSegment(sketch, "E300", {"start": v(10.44, -1.9) * mm, "end": v(10.47, -2) * mm});
            skLineSegment(sketch, "E301", {"start": v(10.47, -2) * mm, "end": v(10.49, -2.08) * mm});
            skLineSegment(sketch, "E302", {"start": v(10.49, -2.08) * mm, "end": v(10.5, -2.17) * mm});
            skLineSegment(sketch, "E303", {"start": v(10.5, -2.17) * mm, "end": v(10.5, -2.25) * mm});
            skLineSegment(sketch, "E304", {"start": v(10.5, -2.25) * mm, "end": v(10.49, -2.33) * mm});
            skLineSegment(sketch, "E305", {"start": v(10.49, -2.33) * mm, "end": v(10.46, -2.4) * mm});
            skLineSegment(sketch, "E306", {"start": v(10.46, -2.4) * mm, "end": v(10.41, -2.47) * mm});
            skLineSegment(sketch, "E307", {"start": v(10.41, -2.47) * mm, "end": v(10.35, -2.53) * mm});
            skLineSegment(sketch, "E308", {"start": v(10.35, -2.53) * mm, "end": v(10.27, -2.58) * mm});
            skLineSegment(sketch, "E309", {"start": v(10.27, -2.58) * mm, "end": v(10.16, -2.62) * mm});
            skLineSegment(sketch, "E310", {"start": v(10.16, -2.62) * mm, "end": v(10.04, -2.65) * mm});
            skLineSegment(sketch, "E311", {"start": v(10.04, -2.65) * mm, "end": v(9.88, -2.67) * mm});
            skLineSegment(sketch, "E312", {"start": v(9.88, -2.67) * mm, "end": v(9.48, -2.67) * mm});
            skLineSegment(sketch, "E313", {"start": v(9.48, -2.67) * mm, "end": v(9.08, -2.61) * mm});
            skLineSegment(sketch, "E314", {"start": v(9.08, -2.61) * mm, "end": v(8.7, -2.5) * mm});
            skLineSegment(sketch, "E315", {"start": v(8.7, -2.5) * mm, "end": v(8.34, -2.32) * mm});
            skLineSegment(sketch, "E316", {"start": v(8.34, -2.32) * mm, "end": v(8, -2.1) * mm});
            skLineSegment(sketch, "E317", {"start": v(8, -2.1) * mm, "end": v(7.69, -1.83) * mm});
            skLineSegment(sketch, "E318", {"start": v(7.69, -1.83) * mm, "end": v(7.41, -1.54) * mm});
            skLineSegment(sketch, "E319", {"start": v(7.41, -1.54) * mm, "end": v(7.17, -1.21) * mm});
            skLineSegment(sketch, "E320", {"start": v(7.17, -1.21) * mm, "end": v(7.02, -1.3) * mm});
            skLineSegment(sketch, "E321", {"start": v(7.02, -1.3) * mm, "end": v(6.87, -1.39) * mm});
            skLineSegment(sketch, "E322", {"start": v(6.87, -1.39) * mm, "end": v(6.72, -1.5) * mm});
            skLineSegment(sketch, "E323", {"start": v(6.72, -1.5) * mm, "end": v(6.58, -1.61) * mm});
            skLineSegment(sketch, "E324", {"start": v(6.58, -1.61) * mm, "end": v(6.44, -1.74) * mm});
            skLineSegment(sketch, "E325", {"start": v(6.44, -1.74) * mm, "end": v(6.3, -1.88) * mm});
            skLineSegment(sketch, "E326", {"start": v(6.3, -1.88) * mm, "end": v(6.17, -2.01) * mm});
            skLineSegment(sketch, "E327", {"start": v(6.17, -2.01) * mm, "end": v(6.03, -2.15) * mm});
            skLineSegment(sketch, "E328", {"start": v(6.03, -2.15) * mm, "end": v(5.9, -2.28) * mm});
            skLineSegment(sketch, "E329", {"start": v(5.9, -2.28) * mm, "end": v(5.75, -2.4) * mm});
            skLineSegment(sketch, "E330", {"start": v(5.75, -2.4) * mm, "end": v(5.6, -2.52) * mm});
            skLineSegment(sketch, "E331", {"start": v(5.6, -2.52) * mm, "end": v(5.44, -2.62) * mm});
            skLineSegment(sketch, "E332", {"start": v(5.44, -2.62) * mm, "end": v(5.28, -2.71) * mm});
            skLineSegment(sketch, "E333", {"start": v(5.28, -2.71) * mm, "end": v(5.1, -2.78) * mm});
            skLineSegment(sketch, "E334", {"start": v(5.1, -2.78) * mm, "end": v(4.92, -2.82) * mm});
            skLineSegment(sketch, "E335", {"start": v(4.92, -2.82) * mm, "end": v(4.73, -2.84) * mm});
            skLineSegment(sketch, "E336", {"start": v(4.73, -2.84) * mm, "end": v(4.39, -3.25) * mm});
            skLineSegment(sketch, "E337", {"start": v(4.39, -3.25) * mm, "end": v(4, -3.63) * mm});
            skLineSegment(sketch, "E338", {"start": v(4, -3.63) * mm, "end": v(3.58, -3.96) * mm});
            skLineSegment(sketch, "E339", {"start": v(3.58, -3.96) * mm, "end": v(3.12, -4.24) * mm});
            skLineSegment(sketch, "E340", {"start": v(3.12, -4.24) * mm, "end": v(2.63, -4.46) * mm});
            skLineSegment(sketch, "E341", {"start": v(2.63, -4.46) * mm, "end": v(2.12, -4.62) * mm});
            skLineSegment(sketch, "E342", {"start": v(2.12, -4.62) * mm, "end": v(1.6, -4.7) * mm});
            skLineSegment(sketch, "E343", {"start": v(1.6, -4.7) * mm, "end": v(1.05, -4.71) * mm});
            skLineSegment(sketch, "E344", {"start": v(1.05, -4.71) * mm, "end": v(1, -4.83) * mm});
            skLineSegment(sketch, "E345", {"start": v(1, -4.83) * mm, "end": v(0.93, -4.93) * mm});
            skLineSegment(sketch, "E346", {"start": v(0.93, -4.93) * mm, "end": v(0.85, -5.04) * mm});
            skLineSegment(sketch, "E347", {"start": v(0.85, -5.04) * mm, "end": v(0.75, -5.15) * mm});
            skLineSegment(sketch, "E348", {"start": v(0.75, -5.15) * mm, "end": v(0.65, -5.25) * mm});
            skLineSegment(sketch, "E349", {"start": v(0.65, -5.25) * mm, "end": v(0.55, -5.35) * mm});
            skLineSegment(sketch, "E350", {"start": v(0.55, -5.35) * mm, "end": v(0.44, -5.45) * mm});
            skLineSegment(sketch, "E351", {"start": v(0.44, -5.45) * mm, "end": v(0.34, -5.56) * mm});
            skLineSegment(sketch, "E352", {"start": v(0.34, -5.56) * mm, "end": v(0.25, -5.66) * mm});
            skLineSegment(sketch, "E353", {"start": v(0.25, -5.66) * mm, "end": v(0.16, -5.76) * mm});
            skLineSegment(sketch, "E354", {"start": v(0.16, -5.76) * mm, "end": v(0.09, -5.87) * mm});
            skLineSegment(sketch, "E355", {"start": v(0.09, -5.87) * mm, "end": v(0.03, -5.98) * mm});
            skLineSegment(sketch, "E356", {"start": v(0.03, -5.98) * mm, "end": v(0, -6.1) * mm});
            skLineSegment(sketch, "E357", {"start": v(0, -6.1) * mm, "end": v(-0.02, -6.2) * mm});
            skLineSegment(sketch, "E358", {"start": v(-0.02, -6.2) * mm, "end": v(0, -6.33) * mm});
            skLineSegment(sketch, "E359", {"start": v(0, -6.33) * mm, "end": v(0.04, -6.45) * mm});
            skLineSegment(sketch, "E360", {"start": v(0.04, -6.45) * mm, "end": v(0.08, -6.54) * mm});
            skLineSegment(sketch, "E361", {"start": v(0.08, -6.54) * mm, "end": v(0.15, -6.64) * mm});
            skLineSegment(sketch, "E362", {"start": v(0.15, -6.64) * mm, "end": v(0.26, -6.75) * mm});
            skLineSegment(sketch, "E363", {"start": v(0.26, -6.75) * mm, "end": v(0.37, -6.88) * mm});
            skLineSegment(sketch, "E364", {"start": v(0.37, -6.88) * mm, "end": v(0.5, -7.01) * mm});
            skLineSegment(sketch, "E365", {"start": v(0.5, -7.01) * mm, "end": v(0.65, -7.15) * mm});
            skLineSegment(sketch, "E366", {"start": v(0.65, -7.15) * mm, "end": v(0.78, -7.3) * mm});
            skLineSegment(sketch, "E367", {"start": v(0.78, -7.3) * mm, "end": v(0.91, -7.44) * mm});
            skLineSegment(sketch, "E368", {"start": v(0.91, -7.44) * mm, "end": v(1.03, -7.58) * mm});
            skLineSegment(sketch, "E369", {"start": v(1.03, -7.58) * mm, "end": v(1.13, -7.71) * mm});
            skLineSegment(sketch, "E370", {"start": v(1.13, -7.71) * mm, "end": v(1.2, -7.84) * mm});
            skLineSegment(sketch, "E371", {"start": v(1.2, -7.84) * mm, "end": v(1.25, -7.95) * mm});
            skLineSegment(sketch, "E372", {"start": v(1.25, -7.95) * mm, "end": v(1.25, -8.05) * mm});
            skLineSegment(sketch, "E373", {"start": v(1.25, -8.05) * mm, "end": v(1.2, -8.14) * mm});
            skLineSegment(sketch, "E374", {"start": v(1.2, -8.14) * mm, "end": v(1.12, -8.2) * mm});
            skLineSegment(sketch, "E375", {"start": v(1.12, -8.2) * mm, "end": v(0.97, -8.24) * mm});
            skCircle(sketch, "E376", {"center": v(0.44, 0.58) * mm, "radius": 14 * mm, "construction": true});
            skSolve(sketch);
        }
        {
            var Q0;
            Q0=makeQuery(id+"F0.imprint","IMPRINT",FACE,{"disambiguationData":[TD([[makeQuery(id+"F0.imprint","IMPRINT",EDGE,{"derivedFrom":sQuery(id+"F0.wireOp",EDGE,"E0")}),-1.0]])]});
            extrude(context, id + "F1", {"entities" : qUnion([Q0]), "depth" : 2.5 * mm, "offsetDistance" : 25 * mm});
        }
        {
            var Q0;
            Q0=makeQuery(id+"F1.opExtrude","CAP_FACE",FACE,{"disambiguationData":[OSD([sQuery(id+"F0.wireOp",EDGE,"E0"),sQuery(id+"F0.wireOp",EDGE,"E1"),sQuery(id+"F0.wireOp",EDGE,"E2"),sQuery(id+"F0.wireOp",EDGE,"E3"),sQuery(id+"F0.wireOp",EDGE,"E4"),sQuery(id+"F0.wireOp",EDGE,"E5"),sQuery(id+"F0.wireOp",EDGE,"E6"),sQuery(id+"F0.wireOp",EDGE,"E7"),sQuery(id+"F0.wireOp",EDGE,"E8"),sQuery(id+"F0.wireOp",EDGE,"E9"),sQuery(id+"F0.wireOp",EDGE,"E10"),sQuery(id+"F0.wireOp",EDGE,"E11"),sQuery(id+"F0.wireOp",EDGE,"E12"),sQuery(id+"F0.wireOp",EDGE,"E13"),sQuery(id+"F0.wireOp",EDGE,"E14"),sQuery(id+"F0.wireOp",EDGE,"E15"),sQuery(id+"F0.wireOp",EDGE,"E16"),sQuery(id+"F0.wireOp",EDGE,"E17"),sQuery(id+"F0.wireOp",EDGE,"E18"),sQuery(id+"F0.wireOp",EDGE,"E19"),sQuery(id+"F0.wireOp",EDGE,"E20"),sQuery(id+"F0.wireOp",EDGE,"E21"),sQuery(id+"F0.wireOp",EDGE,"E22"),sQuery(id+"F0.wireOp",EDGE,"E23"),sQuery(id+"F0.wireOp",EDGE,"E24"),sQuery(id+"F0.wireOp",EDGE,"E25"),sQuery(id+"F0.wireOp",EDGE,"E26"),sQuery(id+"F0.wireOp",EDGE,"E27"),sQuery(id+"F0.wireOp",EDGE,"E28"),sQuery(id+"F0.wireOp",EDGE,"E29"),sQuery(id+"F0.wireOp",EDGE,"E30"),sQuery(id+"F0.wireOp",EDGE,"E31"),sQuery(id+"F0.wireOp",EDGE,"E32"),sQuery(id+"F0.wireOp",EDGE,"E33"),sQuery(id+"F0.wireOp",EDGE,"E34"),sQuery(id+"F0.wireOp",EDGE,"E35"),sQuery(id+"F0.wireOp",EDGE,"E36"),sQuery(id+"F0.wireOp",EDGE,"E37"),sQuery(id+"F0.wireOp",EDGE,"E38"),sQuery(id+"F0.wireOp",EDGE,"E39"),sQuery(id+"F0.wireOp",EDGE,"E40"),sQuery(id+"F0.wireOp",EDGE,"E41"),sQuery(id+"F0.wireOp",EDGE,"E42"),sQuery(id+"F0.wireOp",EDGE,"E43"),sQuery(id+"F0.wireOp",EDGE,"E44"),sQuery(id+"F0.wireOp",EDGE,"E45"),sQuery(id+"F0.wireOp",EDGE,"E46"),sQuery(id+"F0.wireOp",EDGE,"E47"),sQuery(id+"F0.wireOp",EDGE,"E48"),sQuery(id+"F0.wireOp",EDGE,"E49"),sQuery(id+"F0.wireOp",EDGE,"E50"),sQuery(id+"F0.wireOp",EDGE,"E51"),sQuery(id+"F0.wireOp",EDGE,"E52"),sQuery(id+"F0.wireOp",EDGE,"E53"),sQuery(id+"F0.wireOp",EDGE,"E54"),sQuery(id+"F0.wireOp",EDGE,"E55"),sQuery(id+"F0.wireOp",EDGE,"E56"),sQuery(id+"F0.wireOp",EDGE,"E57"),sQuery(id+"F0.wireOp",EDGE,"E58"),sQuery(id+"F0.wireOp",EDGE,"E59"),sQuery(id+"F0.wireOp",EDGE,"E60"),sQuery(id+"F0.wireOp",EDGE,"E61"),sQuery(id+"F0.wireOp",EDGE,"E62"),sQuery(id+"F0.wireOp",EDGE,"E63"),sQuery(id+"F0.wireOp",EDGE,"E64"),sQuery(id+"F0.wireOp",EDGE,"E65"),sQuery(id+"F0.wireOp",EDGE,"E66"),sQuery(id+"F0.wireOp",EDGE,"E67"),sQuery(id+"F0.wireOp",EDGE,"E68"),sQuery(id+"F0.wireOp",EDGE,"E69"),sQuery(id+"F0.wireOp",EDGE,"E70"),sQuery(id+"F0.wireOp",EDGE,"E71"),sQuery(id+"F0.wireOp",EDGE,"E72"),sQuery(id+"F0.wireOp",EDGE,"E73"),sQuery(id+"F0.wireOp",EDGE,"E74"),sQuery(id+"F0.wireOp",EDGE,"E75"),sQuery(id+"F0.wireOp",EDGE,"E76"),sQuery(id+"F0.wireOp",EDGE,"E77"),sQuery(id+"F0.wireOp",EDGE,"E78"),sQuery(id+"F0.wireOp",EDGE,"E79"),sQuery(id+"F0.wireOp",EDGE,"E80"),sQuery(id+"F0.wireOp",EDGE,"E81"),sQuery(id+"F0.wireOp",EDGE,"E82"),sQuery(id+"F0.wireOp",EDGE,"E83"),sQuery(id+"F0.wireOp",EDGE,"E84"),sQuery(id+"F0.wireOp",EDGE,"E85"),sQuery(id+"F0.wireOp",EDGE,"E86"),sQuery(id+"F0.wireOp",EDGE,"E87"),sQuery(id+"F0.wireOp",EDGE,"E88"),sQuery(id+"F0.wireOp",EDGE,"E89"),sQuery(id+"F0.wireOp",EDGE,"E90"),sQuery(id+"F0.wireOp",EDGE,"E91"),sQuery(id+"F0.wireOp",EDGE,"E92"),sQuery(id+"F0.wireOp",EDGE,"E93"),sQuery(id+"F0.wireOp",EDGE,"E94"),sQuery(id+"F0.wireOp",EDGE,"E95"),sQuery(id+"F0.wireOp",EDGE,"E96"),sQuery(id+"F0.wireOp",EDGE,"E97"),sQuery(id+"F0.wireOp",EDGE,"E98"),sQuery(id+"F0.wireOp",EDGE,"E99"),sQuery(id+"F0.wireOp",EDGE,"E100"),sQuery(id+"F0.wireOp",EDGE,"E101"),sQuery(id+"F0.wireOp",EDGE,"E102"),sQuery(id+"F0.wireOp",EDGE,"E103"),sQuery(id+"F0.wireOp",EDGE,"E104"),sQuery(id+"F0.wireOp",EDGE,"E105"),sQuery(id+"F0.wireOp",EDGE,"E106"),sQuery(id+"F0.wireOp",EDGE,"E107"),sQuery(id+"F0.wireOp",EDGE,"E108"),sQuery(id+"F0.wireOp",EDGE,"E109"),sQuery(id+"F0.wireOp",EDGE,"E110"),sQuery(id+"F0.wireOp",EDGE,"E111"),sQuery(id+"F0.wireOp",EDGE,"E112"),sQuery(id+"F0.wireOp",EDGE,"E113"),sQuery(id+"F0.wireOp",EDGE,"E114"),sQuery(id+"F0.wireOp",EDGE,"E115"),sQuery(id+"F0.wireOp",EDGE,"E116"),sQuery(id+"F0.wireOp",EDGE,"E117"),sQuery(id+"F0.wireOp",EDGE,"E118"),sQuery(id+"F0.wireOp",EDGE,"E119"),sQuery(id+"F0.wireOp",EDGE,"E120"),sQuery(id+"F0.wireOp",EDGE,"E121"),sQuery(id+"F0.wireOp",EDGE,"E122"),sQuery(id+"F0.wireOp",EDGE,"E123"),sQuery(id+"F0.wireOp",EDGE,"E124"),sQuery(id+"F0.wireOp",EDGE,"E125"),sQuery(id+"F0.wireOp",EDGE,"E126"),sQuery(id+"F0.wireOp",EDGE,"E127"),sQuery(id+"F0.wireOp",EDGE,"E128"),sQuery(id+"F0.wireOp",EDGE,"E129"),sQuery(id+"F0.wireOp",EDGE,"E130"),sQuery(id+"F0.wireOp",EDGE,"E131"),sQuery(id+"F0.wireOp",EDGE,"E132"),sQuery(id+"F0.wireOp",EDGE,"E133"),sQuery(id+"F0.wireOp",EDGE,"E134"),sQuery(id+"F0.wireOp",EDGE,"E135"),sQuery(id+"F0.wireOp",EDGE,"E136"),sQuery(id+"F0.wireOp",EDGE,"E137"),sQuery(id+"F0.wireOp",EDGE,"E138"),sQuery(id+"F0.wireOp",EDGE,"E139"),sQuery(id+"F0.wireOp",EDGE,"E140"),sQuery(id+"F0.wireOp",EDGE,"E141"),sQuery(id+"F0.wireOp",EDGE,"E142"),sQuery(id+"F0.wireOp",EDGE,"E143"),sQuery(id+"F0.wireOp",EDGE,"E144"),sQuery(id+"F0.wireOp",EDGE,"E145"),sQuery(id+"F0.wireOp",EDGE,"E146"),sQuery(id+"F0.wireOp",EDGE,"E147"),sQuery(id+"F0.wireOp",EDGE,"E148"),sQuery(id+"F0.wireOp",EDGE,"E149"),sQuery(id+"F0.wireOp",EDGE,"E150"),sQuery(id+"F0.wireOp",EDGE,"E151"),sQuery(id+"F0.wireOp",EDGE,"E152"),sQuery(id+"F0.wireOp",EDGE,"E153"),sQuery(id+"F0.wireOp",EDGE,"E154"),sQuery(id+"F0.wireOp",EDGE,"E155"),sQuery(id+"F0.wireOp",EDGE,"E156"),sQuery(id+"F0.wireOp",EDGE,"E157"),sQuery(id+"F0.wireOp",EDGE,"E158"),sQuery(id+"F0.wireOp",EDGE,"E159"),sQuery(id+"F0.wireOp",EDGE,"E160"),sQuery(id+"F0.wireOp",EDGE,"E161"),sQuery(id+"F0.wireOp",EDGE,"E162"),sQuery(id+"F0.wireOp",EDGE,"E163"),sQuery(id+"F0.wireOp",EDGE,"E164"),sQuery(id+"F0.wireOp",EDGE,"E165"),sQuery(id+"F0.wireOp",EDGE,"E166"),sQuery(id+"F0.wireOp",EDGE,"E167"),sQuery(id+"F0.wireOp",EDGE,"E168"),sQuery(id+"F0.wireOp",EDGE,"E169"),sQuery(id+"F0.wireOp",EDGE,"E170"),sQuery(id+"F0.wireOp",EDGE,"E171"),sQuery(id+"F0.wireOp",EDGE,"E172"),sQuery(id+"F0.wireOp",EDGE,"E173"),sQuery(id+"F0.wireOp",EDGE,"E174"),sQuery(id+"F0.wireOp",EDGE,"E175"),sQuery(id+"F0.wireOp",EDGE,"E176"),sQuery(id+"F0.wireOp",EDGE,"E177"),sQuery(id+"F0.wireOp",EDGE,"E178"),sQuery(id+"F0.wireOp",EDGE,"E179"),sQuery(id+"F0.wireOp",EDGE,"E180"),sQuery(id+"F0.wireOp",EDGE,"E181"),sQuery(id+"F0.wireOp",EDGE,"E182"),sQuery(id+"F0.wireOp",EDGE,"E183"),sQuery(id+"F0.wireOp",EDGE,"E184"),sQuery(id+"F0.wireOp",EDGE,"E185"),sQuery(id+"F0.wireOp",EDGE,"E186"),sQuery(id+"F0.wireOp",EDGE,"E187"),sQuery(id+"F0.wireOp",EDGE,"E188"),sQuery(id+"F0.wireOp",EDGE,"E189"),sQuery(id+"F0.wireOp",EDGE,"E190"),sQuery(id+"F0.wireOp",EDGE,"E191"),sQuery(id+"F0.wireOp",EDGE,"E192"),sQuery(id+"F0.wireOp",EDGE,"E193"),sQuery(id+"F0.wireOp",EDGE,"E194"),sQuery(id+"F0.wireOp",EDGE,"E195"),sQuery(id+"F0.wireOp",EDGE,"E196"),sQuery(id+"F0.wireOp",EDGE,"E197"),sQuery(id+"F0.wireOp",EDGE,"E198"),sQuery(id+"F0.wireOp",EDGE,"E199"),sQuery(id+"F0.wireOp",EDGE,"E200"),sQuery(id+"F0.wireOp",EDGE,"E201"),sQuery(id+"F0.wireOp",EDGE,"E202"),sQuery(id+"F0.wireOp",EDGE,"E203"),sQuery(id+"F0.wireOp",EDGE,"E204"),sQuery(id+"F0.wireOp",EDGE,"E205"),sQuery(id+"F0.wireOp",EDGE,"E206"),sQuery(id+"F0.wireOp",EDGE,"E207"),sQuery(id+"F0.wireOp",EDGE,"E208"),sQuery(id+"F0.wireOp",EDGE,"E209"),sQuery(id+"F0.wireOp",EDGE,"E210"),sQuery(id+"F0.wireOp",EDGE,"E211"),sQuery(id+"F0.wireOp",EDGE,"E212"),sQuery(id+"F0.wireOp",EDGE,"E213"),sQuery(id+"F0.wireOp",EDGE,"E214"),sQuery(id+"F0.wireOp",EDGE,"E215"),sQuery(id+"F0.wireOp",EDGE,"E216"),sQuery(id+"F0.wireOp",EDGE,"E217"),sQuery(id+"F0.wireOp",EDGE,"E218"),sQuery(id+"F0.wireOp",EDGE,"E219"),sQuery(id+"F0.wireOp",EDGE,"E220"),sQuery(id+"F0.wireOp",EDGE,"E221"),sQuery(id+"F0.wireOp",EDGE,"E222"),sQuery(id+"F0.wireOp",EDGE,"E223"),sQuery(id+"F0.wireOp",EDGE,"E224"),sQuery(id+"F0.wireOp",EDGE,"E225"),sQuery(id+"F0.wireOp",EDGE,"E226"),sQuery(id+"F0.wireOp",EDGE,"E227"),sQuery(id+"F0.wireOp",EDGE,"E228"),sQuery(id+"F0.wireOp",EDGE,"E229"),sQuery(id+"F0.wireOp",EDGE,"E230"),sQuery(id+"F0.wireOp",EDGE,"E231"),sQuery(id+"F0.wireOp",EDGE,"E232"),sQuery(id+"F0.wireOp",EDGE,"E233"),sQuery(id+"F0.wireOp",EDGE,"E234"),sQuery(id+"F0.wireOp",EDGE,"E235"),sQuery(id+"F0.wireOp",EDGE,"E236"),sQuery(id+"F0.wireOp",EDGE,"E237"),sQuery(id+"F0.wireOp",EDGE,"E238"),sQuery(id+"F0.wireOp",EDGE,"E239"),sQuery(id+"F0.wireOp",EDGE,"E240"),sQuery(id+"F0.wireOp",EDGE,"E241"),sQuery(id+"F0.wireOp",EDGE,"E242"),sQuery(id+"F0.wireOp",EDGE,"E243"),sQuery(id+"F0.wireOp",EDGE,"E244"),sQuery(id+"F0.wireOp",EDGE,"E245"),sQuery(id+"F0.wireOp",EDGE,"E246"),sQuery(id+"F0.wireOp",EDGE,"E247"),sQuery(id+"F0.wireOp",EDGE,"E248"),sQuery(id+"F0.wireOp",EDGE,"E249"),sQuery(id+"F0.wireOp",EDGE,"E250"),sQuery(id+"F0.wireOp",EDGE,"E251"),sQuery(id+"F0.wireOp",EDGE,"E252"),sQuery(id+"F0.wireOp",EDGE,"E253"),sQuery(id+"F0.wireOp",EDGE,"E254"),sQuery(id+"F0.wireOp",EDGE,"E255"),sQuery(id+"F0.wireOp",EDGE,"E256"),sQuery(id+"F0.wireOp",EDGE,"E257"),sQuery(id+"F0.wireOp",EDGE,"E258"),sQuery(id+"F0.wireOp",EDGE,"E259"),sQuery(id+"F0.wireOp",EDGE,"E260"),sQuery(id+"F0.wireOp",EDGE,"E261"),sQuery(id+"F0.wireOp",EDGE,"E262"),sQuery(id+"F0.wireOp",EDGE,"E263"),sQuery(id+"F0.wireOp",EDGE,"E264"),sQuery(id+"F0.wireOp",EDGE,"E265"),sQuery(id+"F0.wireOp",EDGE,"E266"),sQuery(id+"F0.wireOp",EDGE,"E267"),sQuery(id+"F0.wireOp",EDGE,"E268"),sQuery(id+"F0.wireOp",EDGE,"E269"),sQuery(id+"F0.wireOp",EDGE,"E270"),sQuery(id+"F0.wireOp",EDGE,"E271"),sQuery(id+"F0.wireOp",EDGE,"E272"),sQuery(id+"F0.wireOp",EDGE,"E273"),sQuery(id+"F0.wireOp",EDGE,"E274"),sQuery(id+"F0.wireOp",EDGE,"E275"),sQuery(id+"F0.wireOp",EDGE,"E276"),sQuery(id+"F0.wireOp",EDGE,"E277"),sQuery(id+"F0.wireOp",EDGE,"E278"),sQuery(id+"F0.wireOp",EDGE,"E279"),sQuery(id+"F0.wireOp",EDGE,"E280"),sQuery(id+"F0.wireOp",EDGE,"E281"),sQuery(id+"F0.wireOp",EDGE,"E282"),sQuery(id+"F0.wireOp",EDGE,"E283"),sQuery(id+"F0.wireOp",EDGE,"E284"),sQuery(id+"F0.wireOp",EDGE,"E285"),sQuery(id+"F0.wireOp",EDGE,"E286"),sQuery(id+"F0.wireOp",EDGE,"E287"),sQuery(id+"F0.wireOp",EDGE,"E288"),sQuery(id+"F0.wireOp",EDGE,"E289"),sQuery(id+"F0.wireOp",EDGE,"E290"),sQuery(id+"F0.wireOp",EDGE,"E291"),sQuery(id+"F0.wireOp",EDGE,"E292"),sQuery(id+"F0.wireOp",EDGE,"E293"),sQuery(id+"F0.wireOp",EDGE,"E294"),sQuery(id+"F0.wireOp",EDGE,"E295"),sQuery(id+"F0.wireOp",EDGE,"E296"),sQuery(id+"F0.wireOp",EDGE,"E297"),sQuery(id+"F0.wireOp",EDGE,"E298"),sQuery(id+"F0.wireOp",EDGE,"E299"),sQuery(id+"F0.wireOp",EDGE,"E300"),sQuery(id+"F0.wireOp",EDGE,"E301"),sQuery(id+"F0.wireOp",EDGE,"E302"),sQuery(id+"F0.wireOp",EDGE,"E303"),sQuery(id+"F0.wireOp",EDGE,"E304"),sQuery(id+"F0.wireOp",EDGE,"E305"),sQuery(id+"F0.wireOp",EDGE,"E306"),sQuery(id+"F0.wireOp",EDGE,"E307"),sQuery(id+"F0.wireOp",EDGE,"E308"),sQuery(id+"F0.wireOp",EDGE,"E309"),sQuery(id+"F0.wireOp",EDGE,"E310"),sQuery(id+"F0.wireOp",EDGE,"E311"),sQuery(id+"F0.wireOp",EDGE,"E312"),sQuery(id+"F0.wireOp",EDGE,"E313"),sQuery(id+"F0.wireOp",EDGE,"E314"),sQuery(id+"F0.wireOp",EDGE,"E315"),sQuery(id+"F0.wireOp",EDGE,"E316"),sQuery(id+"F0.wireOp",EDGE,"E317"),sQuery(id+"F0.wireOp",EDGE,"E318"),sQuery(id+"F0.wireOp",EDGE,"E319"),sQuery(id+"F0.wireOp",EDGE,"E320"),sQuery(id+"F0.wireOp",EDGE,"E321"),sQuery(id+"F0.wireOp",EDGE,"E322"),sQuery(id+"F0.wireOp",EDGE,"E323"),sQuery(id+"F0.wireOp",EDGE,"E324"),sQuery(id+"F0.wireOp",EDGE,"E325"),sQuery(id+"F0.wireOp",EDGE,"E326"),sQuery(id+"F0.wireOp",EDGE,"E327"),sQuery(id+"F0.wireOp",EDGE,"E328"),sQuery(id+"F0.wireOp",EDGE,"E329"),sQuery(id+"F0.wireOp",EDGE,"E330"),sQuery(id+"F0.wireOp",EDGE,"E331"),sQuery(id+"F0.wireOp",EDGE,"E332"),sQuery(id+"F0.wireOp",EDGE,"E333"),sQuery(id+"F0.wireOp",EDGE,"E334"),sQuery(id+"F0.wireOp",EDGE,"E335"),sQuery(id+"F0.wireOp",EDGE,"E336"),sQuery(id+"F0.wireOp",EDGE,"E337"),sQuery(id+"F0.wireOp",EDGE,"E338"),sQuery(id+"F0.wireOp",EDGE,"E339"),sQuery(id+"F0.wireOp",EDGE,"E340"),sQuery(id+"F0.wireOp",EDGE,"E341"),sQuery(id+"F0.wireOp",EDGE,"E342"),sQuery(id+"F0.wireOp",EDGE,"E343"),sQuery(id+"F0.wireOp",EDGE,"E344"),sQuery(id+"F0.wireOp",EDGE,"E345"),sQuery(id+"F0.wireOp",EDGE,"E346"),sQuery(id+"F0.wireOp",EDGE,"E347"),sQuery(id+"F0.wireOp",EDGE,"E348"),sQuery(id+"F0.wireOp",EDGE,"E349"),sQuery(id+"F0.wireOp",EDGE,"E350"),sQuery(id+"F0.wireOp",EDGE,"E351"),sQuery(id+"F0.wireOp",EDGE,"E352"),sQuery(id+"F0.wireOp",EDGE,"E353"),sQuery(id+"F0.wireOp",EDGE,"E354"),sQuery(id+"F0.wireOp",EDGE,"E355"),sQuery(id+"F0.wireOp",EDGE,"E356"),sQuery(id+"F0.wireOp",EDGE,"E357"),sQuery(id+"F0.wireOp",EDGE,"E358"),sQuery(id+"F0.wireOp",EDGE,"E359"),sQuery(id+"F0.wireOp",EDGE,"E360"),sQuery(id+"F0.wireOp",EDGE,"E361"),sQuery(id+"F0.wireOp",EDGE,"E362"),sQuery(id+"F0.wireOp",EDGE,"E363"),sQuery(id+"F0.wireOp",EDGE,"E364"),sQuery(id+"F0.wireOp",EDGE,"E365"),sQuery(id+"F0.wireOp",EDGE,"E366"),sQuery(id+"F0.wireOp",EDGE,"E367"),sQuery(id+"F0.wireOp",EDGE,"E368"),sQuery(id+"F0.wireOp",EDGE,"E369"),sQuery(id+"F0.wireOp",EDGE,"E370"),sQuery(id+"F0.wireOp",EDGE,"E371"),sQuery(id+"F0.wireOp",EDGE,"E372"),sQuery(id+"F0.wireOp",EDGE,"E373"),sQuery(id+"F0.wireOp",EDGE,"E374"),sQuery(id+"F0.wireOp",EDGE,"E375")])],"isStart":true});
            chamfer(context, id + "F2", {"entities" : qUnion([Q0]), "width" : 0.12 * mm, "tangentPropagation" : true});
        }
        {
            var Q0;
            Q0=makeQuery(id+"F1.opExtrude","CAP_FACE",FACE,{"disambiguationData":[OSD([sQuery(id+"F0.wireOp",EDGE,"E0"),sQuery(id+"F0.wireOp",EDGE,"E1"),sQuery(id+"F0.wireOp",EDGE,"E2"),sQuery(id+"F0.wireOp",EDGE,"E3"),sQuery(id+"F0.wireOp",EDGE,"E4"),sQuery(id+"F0.wireOp",EDGE,"E5"),sQuery(id+"F0.wireOp",EDGE,"E6"),sQuery(id+"F0.wireOp",EDGE,"E7"),sQuery(id+"F0.wireOp",EDGE,"E8"),sQuery(id+"F0.wireOp",EDGE,"E9"),sQuery(id+"F0.wireOp",EDGE,"E10"),sQuery(id+"F0.wireOp",EDGE,"E11"),sQuery(id+"F0.wireOp",EDGE,"E12"),sQuery(id+"F0.wireOp",EDGE,"E13"),sQuery(id+"F0.wireOp",EDGE,"E14"),sQuery(id+"F0.wireOp",EDGE,"E15"),sQuery(id+"F0.wireOp",EDGE,"E16"),sQuery(id+"F0.wireOp",EDGE,"E17"),sQuery(id+"F0.wireOp",EDGE,"E18"),sQuery(id+"F0.wireOp",EDGE,"E19"),sQuery(id+"F0.wireOp",EDGE,"E20"),sQuery(id+"F0.wireOp",EDGE,"E21"),sQuery(id+"F0.wireOp",EDGE,"E22"),sQuery(id+"F0.wireOp",EDGE,"E23"),sQuery(id+"F0.wireOp",EDGE,"E24"),sQuery(id+"F0.wireOp",EDGE,"E25"),sQuery(id+"F0.wireOp",EDGE,"E26"),sQuery(id+"F0.wireOp",EDGE,"E27"),sQuery(id+"F0.wireOp",EDGE,"E28"),sQuery(id+"F0.wireOp",EDGE,"E29"),sQuery(id+"F0.wireOp",EDGE,"E30"),sQuery(id+"F0.wireOp",EDGE,"E31"),sQuery(id+"F0.wireOp",EDGE,"E32"),sQuery(id+"F0.wireOp",EDGE,"E33"),sQuery(id+"F0.wireOp",EDGE,"E34"),sQuery(id+"F0.wireOp",EDGE,"E35"),sQuery(id+"F0.wireOp",EDGE,"E36"),sQuery(id+"F0.wireOp",EDGE,"E37"),sQuery(id+"F0.wireOp",EDGE,"E38"),sQuery(id+"F0.wireOp",EDGE,"E39"),sQuery(id+"F0.wireOp",EDGE,"E40"),sQuery(id+"F0.wireOp",EDGE,"E41"),sQuery(id+"F0.wireOp",EDGE,"E42"),sQuery(id+"F0.wireOp",EDGE,"E43"),sQuery(id+"F0.wireOp",EDGE,"E44"),sQuery(id+"F0.wireOp",EDGE,"E45"),sQuery(id+"F0.wireOp",EDGE,"E46"),sQuery(id+"F0.wireOp",EDGE,"E47"),sQuery(id+"F0.wireOp",EDGE,"E48"),sQuery(id+"F0.wireOp",EDGE,"E49"),sQuery(id+"F0.wireOp",EDGE,"E50"),sQuery(id+"F0.wireOp",EDGE,"E51"),sQuery(id+"F0.wireOp",EDGE,"E52"),sQuery(id+"F0.wireOp",EDGE,"E53"),sQuery(id+"F0.wireOp",EDGE,"E54"),sQuery(id+"F0.wireOp",EDGE,"E55"),sQuery(id+"F0.wireOp",EDGE,"E56"),sQuery(id+"F0.wireOp",EDGE,"E57"),sQuery(id+"F0.wireOp",EDGE,"E58"),sQuery(id+"F0.wireOp",EDGE,"E59"),sQuery(id+"F0.wireOp",EDGE,"E60"),sQuery(id+"F0.wireOp",EDGE,"E61"),sQuery(id+"F0.wireOp",EDGE,"E62"),sQuery(id+"F0.wireOp",EDGE,"E63"),sQuery(id+"F0.wireOp",EDGE,"E64"),sQuery(id+"F0.wireOp",EDGE,"E65"),sQuery(id+"F0.wireOp",EDGE,"E66"),sQuery(id+"F0.wireOp",EDGE,"E67"),sQuery(id+"F0.wireOp",EDGE,"E68"),sQuery(id+"F0.wireOp",EDGE,"E69"),sQuery(id+"F0.wireOp",EDGE,"E70"),sQuery(id+"F0.wireOp",EDGE,"E71"),sQuery(id+"F0.wireOp",EDGE,"E72"),sQuery(id+"F0.wireOp",EDGE,"E73"),sQuery(id+"F0.wireOp",EDGE,"E74"),sQuery(id+"F0.wireOp",EDGE,"E75"),sQuery(id+"F0.wireOp",EDGE,"E76"),sQuery(id+"F0.wireOp",EDGE,"E77"),sQuery(id+"F0.wireOp",EDGE,"E78"),sQuery(id+"F0.wireOp",EDGE,"E79"),sQuery(id+"F0.wireOp",EDGE,"E80"),sQuery(id+"F0.wireOp",EDGE,"E81"),sQuery(id+"F0.wireOp",EDGE,"E82"),sQuery(id+"F0.wireOp",EDGE,"E83"),sQuery(id+"F0.wireOp",EDGE,"E84"),sQuery(id+"F0.wireOp",EDGE,"E85"),sQuery(id+"F0.wireOp",EDGE,"E86"),sQuery(id+"F0.wireOp",EDGE,"E87"),sQuery(id+"F0.wireOp",EDGE,"E88"),sQuery(id+"F0.wireOp",EDGE,"E89"),sQuery(id+"F0.wireOp",EDGE,"E90"),sQuery(id+"F0.wireOp",EDGE,"E91"),sQuery(id+"F0.wireOp",EDGE,"E92"),sQuery(id+"F0.wireOp",EDGE,"E93"),sQuery(id+"F0.wireOp",EDGE,"E94"),sQuery(id+"F0.wireOp",EDGE,"E95"),sQuery(id+"F0.wireOp",EDGE,"E96"),sQuery(id+"F0.wireOp",EDGE,"E97"),sQuery(id+"F0.wireOp",EDGE,"E98"),sQuery(id+"F0.wireOp",EDGE,"E99"),sQuery(id+"F0.wireOp",EDGE,"E100"),sQuery(id+"F0.wireOp",EDGE,"E101"),sQuery(id+"F0.wireOp",EDGE,"E102"),sQuery(id+"F0.wireOp",EDGE,"E103"),sQuery(id+"F0.wireOp",EDGE,"E104"),sQuery(id+"F0.wireOp",EDGE,"E105"),sQuery(id+"F0.wireOp",EDGE,"E106"),sQuery(id+"F0.wireOp",EDGE,"E107"),sQuery(id+"F0.wireOp",EDGE,"E108"),sQuery(id+"F0.wireOp",EDGE,"E109"),sQuery(id+"F0.wireOp",EDGE,"E110"),sQuery(id+"F0.wireOp",EDGE,"E111"),sQuery(id+"F0.wireOp",EDGE,"E112"),sQuery(id+"F0.wireOp",EDGE,"E113"),sQuery(id+"F0.wireOp",EDGE,"E114"),sQuery(id+"F0.wireOp",EDGE,"E115"),sQuery(id+"F0.wireOp",EDGE,"E116"),sQuery(id+"F0.wireOp",EDGE,"E117"),sQuery(id+"F0.wireOp",EDGE,"E118"),sQuery(id+"F0.wireOp",EDGE,"E119"),sQuery(id+"F0.wireOp",EDGE,"E120"),sQuery(id+"F0.wireOp",EDGE,"E121"),sQuery(id+"F0.wireOp",EDGE,"E122"),sQuery(id+"F0.wireOp",EDGE,"E123"),sQuery(id+"F0.wireOp",EDGE,"E124"),sQuery(id+"F0.wireOp",EDGE,"E125"),sQuery(id+"F0.wireOp",EDGE,"E126"),sQuery(id+"F0.wireOp",EDGE,"E127"),sQuery(id+"F0.wireOp",EDGE,"E128"),sQuery(id+"F0.wireOp",EDGE,"E129"),sQuery(id+"F0.wireOp",EDGE,"E130"),sQuery(id+"F0.wireOp",EDGE,"E131"),sQuery(id+"F0.wireOp",EDGE,"E132"),sQuery(id+"F0.wireOp",EDGE,"E133"),sQuery(id+"F0.wireOp",EDGE,"E134"),sQuery(id+"F0.wireOp",EDGE,"E135"),sQuery(id+"F0.wireOp",EDGE,"E136"),sQuery(id+"F0.wireOp",EDGE,"E137"),sQuery(id+"F0.wireOp",EDGE,"E138"),sQuery(id+"F0.wireOp",EDGE,"E139"),sQuery(id+"F0.wireOp",EDGE,"E140"),sQuery(id+"F0.wireOp",EDGE,"E141"),sQuery(id+"F0.wireOp",EDGE,"E142"),sQuery(id+"F0.wireOp",EDGE,"E143"),sQuery(id+"F0.wireOp",EDGE,"E144"),sQuery(id+"F0.wireOp",EDGE,"E145"),sQuery(id+"F0.wireOp",EDGE,"E146"),sQuery(id+"F0.wireOp",EDGE,"E147"),sQuery(id+"F0.wireOp",EDGE,"E148"),sQuery(id+"F0.wireOp",EDGE,"E149"),sQuery(id+"F0.wireOp",EDGE,"E150"),sQuery(id+"F0.wireOp",EDGE,"E151"),sQuery(id+"F0.wireOp",EDGE,"E152"),sQuery(id+"F0.wireOp",EDGE,"E153"),sQuery(id+"F0.wireOp",EDGE,"E154"),sQuery(id+"F0.wireOp",EDGE,"E155"),sQuery(id+"F0.wireOp",EDGE,"E156"),sQuery(id+"F0.wireOp",EDGE,"E157"),sQuery(id+"F0.wireOp",EDGE,"E158"),sQuery(id+"F0.wireOp",EDGE,"E159"),sQuery(id+"F0.wireOp",EDGE,"E160"),sQuery(id+"F0.wireOp",EDGE,"E161"),sQuery(id+"F0.wireOp",EDGE,"E162"),sQuery(id+"F0.wireOp",EDGE,"E163"),sQuery(id+"F0.wireOp",EDGE,"E164"),sQuery(id+"F0.wireOp",EDGE,"E165"),sQuery(id+"F0.wireOp",EDGE,"E166"),sQuery(id+"F0.wireOp",EDGE,"E167"),sQuery(id+"F0.wireOp",EDGE,"E168"),sQuery(id+"F0.wireOp",EDGE,"E169"),sQuery(id+"F0.wireOp",EDGE,"E170"),sQuery(id+"F0.wireOp",EDGE,"E171"),sQuery(id+"F0.wireOp",EDGE,"E172"),sQuery(id+"F0.wireOp",EDGE,"E173"),sQuery(id+"F0.wireOp",EDGE,"E174"),sQuery(id+"F0.wireOp",EDGE,"E175"),sQuery(id+"F0.wireOp",EDGE,"E176"),sQuery(id+"F0.wireOp",EDGE,"E177"),sQuery(id+"F0.wireOp",EDGE,"E178"),sQuery(id+"F0.wireOp",EDGE,"E179"),sQuery(id+"F0.wireOp",EDGE,"E180"),sQuery(id+"F0.wireOp",EDGE,"E181"),sQuery(id+"F0.wireOp",EDGE,"E182"),sQuery(id+"F0.wireOp",EDGE,"E183"),sQuery(id+"F0.wireOp",EDGE,"E184"),sQuery(id+"F0.wireOp",EDGE,"E185"),sQuery(id+"F0.wireOp",EDGE,"E186"),sQuery(id+"F0.wireOp",EDGE,"E187"),sQuery(id+"F0.wireOp",EDGE,"E188"),sQuery(id+"F0.wireOp",EDGE,"E189"),sQuery(id+"F0.wireOp",EDGE,"E190"),sQuery(id+"F0.wireOp",EDGE,"E191"),sQuery(id+"F0.wireOp",EDGE,"E192"),sQuery(id+"F0.wireOp",EDGE,"E193"),sQuery(id+"F0.wireOp",EDGE,"E194"),sQuery(id+"F0.wireOp",EDGE,"E195"),sQuery(id+"F0.wireOp",EDGE,"E196"),sQuery(id+"F0.wireOp",EDGE,"E197"),sQuery(id+"F0.wireOp",EDGE,"E198"),sQuery(id+"F0.wireOp",EDGE,"E199"),sQuery(id+"F0.wireOp",EDGE,"E200"),sQuery(id+"F0.wireOp",EDGE,"E201"),sQuery(id+"F0.wireOp",EDGE,"E202"),sQuery(id+"F0.wireOp",EDGE,"E203"),sQuery(id+"F0.wireOp",EDGE,"E204"),sQuery(id+"F0.wireOp",EDGE,"E205"),sQuery(id+"F0.wireOp",EDGE,"E206"),sQuery(id+"F0.wireOp",EDGE,"E207"),sQuery(id+"F0.wireOp",EDGE,"E208"),sQuery(id+"F0.wireOp",EDGE,"E209"),sQuery(id+"F0.wireOp",EDGE,"E210"),sQuery(id+"F0.wireOp",EDGE,"E211"),sQuery(id+"F0.wireOp",EDGE,"E212"),sQuery(id+"F0.wireOp",EDGE,"E213"),sQuery(id+"F0.wireOp",EDGE,"E214"),sQuery(id+"F0.wireOp",EDGE,"E215"),sQuery(id+"F0.wireOp",EDGE,"E216"),sQuery(id+"F0.wireOp",EDGE,"E217"),sQuery(id+"F0.wireOp",EDGE,"E218"),sQuery(id+"F0.wireOp",EDGE,"E219"),sQuery(id+"F0.wireOp",EDGE,"E220"),sQuery(id+"F0.wireOp",EDGE,"E221"),sQuery(id+"F0.wireOp",EDGE,"E222"),sQuery(id+"F0.wireOp",EDGE,"E223"),sQuery(id+"F0.wireOp",EDGE,"E224"),sQuery(id+"F0.wireOp",EDGE,"E225"),sQuery(id+"F0.wireOp",EDGE,"E226"),sQuery(id+"F0.wireOp",EDGE,"E227"),sQuery(id+"F0.wireOp",EDGE,"E228"),sQuery(id+"F0.wireOp",EDGE,"E229"),sQuery(id+"F0.wireOp",EDGE,"E230"),sQuery(id+"F0.wireOp",EDGE,"E231"),sQuery(id+"F0.wireOp",EDGE,"E232"),sQuery(id+"F0.wireOp",EDGE,"E233"),sQuery(id+"F0.wireOp",EDGE,"E234"),sQuery(id+"F0.wireOp",EDGE,"E235"),sQuery(id+"F0.wireOp",EDGE,"E236"),sQuery(id+"F0.wireOp",EDGE,"E237"),sQuery(id+"F0.wireOp",EDGE,"E238"),sQuery(id+"F0.wireOp",EDGE,"E239"),sQuery(id+"F0.wireOp",EDGE,"E240"),sQuery(id+"F0.wireOp",EDGE,"E241"),sQuery(id+"F0.wireOp",EDGE,"E242"),sQuery(id+"F0.wireOp",EDGE,"E243"),sQuery(id+"F0.wireOp",EDGE,"E244"),sQuery(id+"F0.wireOp",EDGE,"E245"),sQuery(id+"F0.wireOp",EDGE,"E246"),sQuery(id+"F0.wireOp",EDGE,"E247"),sQuery(id+"F0.wireOp",EDGE,"E248"),sQuery(id+"F0.wireOp",EDGE,"E249"),sQuery(id+"F0.wireOp",EDGE,"E250"),sQuery(id+"F0.wireOp",EDGE,"E251"),sQuery(id+"F0.wireOp",EDGE,"E252"),sQuery(id+"F0.wireOp",EDGE,"E253"),sQuery(id+"F0.wireOp",EDGE,"E254"),sQuery(id+"F0.wireOp",EDGE,"E255"),sQuery(id+"F0.wireOp",EDGE,"E256"),sQuery(id+"F0.wireOp",EDGE,"E257"),sQuery(id+"F0.wireOp",EDGE,"E258"),sQuery(id+"F0.wireOp",EDGE,"E259"),sQuery(id+"F0.wireOp",EDGE,"E260"),sQuery(id+"F0.wireOp",EDGE,"E261"),sQuery(id+"F0.wireOp",EDGE,"E262"),sQuery(id+"F0.wireOp",EDGE,"E263"),sQuery(id+"F0.wireOp",EDGE,"E264"),sQuery(id+"F0.wireOp",EDGE,"E265"),sQuery(id+"F0.wireOp",EDGE,"E266"),sQuery(id+"F0.wireOp",EDGE,"E267"),sQuery(id+"F0.wireOp",EDGE,"E268"),sQuery(id+"F0.wireOp",EDGE,"E269"),sQuery(id+"F0.wireOp",EDGE,"E270"),sQuery(id+"F0.wireOp",EDGE,"E271"),sQuery(id+"F0.wireOp",EDGE,"E272"),sQuery(id+"F0.wireOp",EDGE,"E273"),sQuery(id+"F0.wireOp",EDGE,"E274"),sQuery(id+"F0.wireOp",EDGE,"E275"),sQuery(id+"F0.wireOp",EDGE,"E276"),sQuery(id+"F0.wireOp",EDGE,"E277"),sQuery(id+"F0.wireOp",EDGE,"E278"),sQuery(id+"F0.wireOp",EDGE,"E279"),sQuery(id+"F0.wireOp",EDGE,"E280"),sQuery(id+"F0.wireOp",EDGE,"E281"),sQuery(id+"F0.wireOp",EDGE,"E282"),sQuery(id+"F0.wireOp",EDGE,"E283"),sQuery(id+"F0.wireOp",EDGE,"E284"),sQuery(id+"F0.wireOp",EDGE,"E285"),sQuery(id+"F0.wireOp",EDGE,"E286"),sQuery(id+"F0.wireOp",EDGE,"E287"),sQuery(id+"F0.wireOp",EDGE,"E288"),sQuery(id+"F0.wireOp",EDGE,"E289"),sQuery(id+"F0.wireOp",EDGE,"E290"),sQuery(id+"F0.wireOp",EDGE,"E291"),sQuery(id+"F0.wireOp",EDGE,"E292"),sQuery(id+"F0.wireOp",EDGE,"E293"),sQuery(id+"F0.wireOp",EDGE,"E294"),sQuery(id+"F0.wireOp",EDGE,"E295"),sQuery(id+"F0.wireOp",EDGE,"E296"),sQuery(id+"F0.wireOp",EDGE,"E297"),sQuery(id+"F0.wireOp",EDGE,"E298"),sQuery(id+"F0.wireOp",EDGE,"E299"),sQuery(id+"F0.wireOp",EDGE,"E300"),sQuery(id+"F0.wireOp",EDGE,"E301"),sQuery(id+"F0.wireOp",EDGE,"E302"),sQuery(id+"F0.wireOp",EDGE,"E303"),sQuery(id+"F0.wireOp",EDGE,"E304"),sQuery(id+"F0.wireOp",EDGE,"E305"),sQuery(id+"F0.wireOp",EDGE,"E306"),sQuery(id+"F0.wireOp",EDGE,"E307"),sQuery(id+"F0.wireOp",EDGE,"E308"),sQuery(id+"F0.wireOp",EDGE,"E309"),sQuery(id+"F0.wireOp",EDGE,"E310"),sQuery(id+"F0.wireOp",EDGE,"E311"),sQuery(id+"F0.wireOp",EDGE,"E312"),sQuery(id+"F0.wireOp",EDGE,"E313"),sQuery(id+"F0.wireOp",EDGE,"E314"),sQuery(id+"F0.wireOp",EDGE,"E315"),sQuery(id+"F0.wireOp",EDGE,"E316"),sQuery(id+"F0.wireOp",EDGE,"E317"),sQuery(id+"F0.wireOp",EDGE,"E318"),sQuery(id+"F0.wireOp",EDGE,"E319"),sQuery(id+"F0.wireOp",EDGE,"E320"),sQuery(id+"F0.wireOp",EDGE,"E321"),sQuery(id+"F0.wireOp",EDGE,"E322"),sQuery(id+"F0.wireOp",EDGE,"E323"),sQuery(id+"F0.wireOp",EDGE,"E324"),sQuery(id+"F0.wireOp",EDGE,"E325"),sQuery(id+"F0.wireOp",EDGE,"E326"),sQuery(id+"F0.wireOp",EDGE,"E327"),sQuery(id+"F0.wireOp",EDGE,"E328"),sQuery(id+"F0.wireOp",EDGE,"E329"),sQuery(id+"F0.wireOp",EDGE,"E330"),sQuery(id+"F0.wireOp",EDGE,"E331"),sQuery(id+"F0.wireOp",EDGE,"E332"),sQuery(id+"F0.wireOp",EDGE,"E333"),sQuery(id+"F0.wireOp",EDGE,"E334"),sQuery(id+"F0.wireOp",EDGE,"E335"),sQuery(id+"F0.wireOp",EDGE,"E336"),sQuery(id+"F0.wireOp",EDGE,"E337"),sQuery(id+"F0.wireOp",EDGE,"E338"),sQuery(id+"F0.wireOp",EDGE,"E339"),sQuery(id+"F0.wireOp",EDGE,"E340"),sQuery(id+"F0.wireOp",EDGE,"E341"),sQuery(id+"F0.wireOp",EDGE,"E342"),sQuery(id+"F0.wireOp",EDGE,"E343"),sQuery(id+"F0.wireOp",EDGE,"E344"),sQuery(id+"F0.wireOp",EDGE,"E345"),sQuery(id+"F0.wireOp",EDGE,"E346"),sQuery(id+"F0.wireOp",EDGE,"E347"),sQuery(id+"F0.wireOp",EDGE,"E348"),sQuery(id+"F0.wireOp",EDGE,"E349"),sQuery(id+"F0.wireOp",EDGE,"E350"),sQuery(id+"F0.wireOp",EDGE,"E351"),sQuery(id+"F0.wireOp",EDGE,"E352"),sQuery(id+"F0.wireOp",EDGE,"E353"),sQuery(id+"F0.wireOp",EDGE,"E354"),sQuery(id+"F0.wireOp",EDGE,"E355"),sQuery(id+"F0.wireOp",EDGE,"E356"),sQuery(id+"F0.wireOp",EDGE,"E357"),sQuery(id+"F0.wireOp",EDGE,"E358"),sQuery(id+"F0.wireOp",EDGE,"E359"),sQuery(id+"F0.wireOp",EDGE,"E360"),sQuery(id+"F0.wireOp",EDGE,"E361"),sQuery(id+"F0.wireOp",EDGE,"E362"),sQuery(id+"F0.wireOp",EDGE,"E363"),sQuery(id+"F0.wireOp",EDGE,"E364"),sQuery(id+"F0.wireOp",EDGE,"E365"),sQuery(id+"F0.wireOp",EDGE,"E366"),sQuery(id+"F0.wireOp",EDGE,"E367"),sQuery(id+"F0.wireOp",EDGE,"E368"),sQuery(id+"F0.wireOp",EDGE,"E369"),sQuery(id+"F0.wireOp",EDGE,"E370"),sQuery(id+"F0.wireOp",EDGE,"E371"),sQuery(id+"F0.wireOp",EDGE,"E372"),sQuery(id+"F0.wireOp",EDGE,"E373"),sQuery(id+"F0.wireOp",EDGE,"E374"),sQuery(id+"F0.wireOp",EDGE,"E375")])],"isStart":false});
            var sketch = newSketch(context, id + "F3", { "sketchPlane" : qUnion([Q0])});
            skCircle(sketch, "E377", {"center": v(-0.74, 4.12) * mm, "radius": 2.6 * mm});
            skCircle(sketch, "E378", {"center": v(-0.74, 4.12) * mm, "radius": 1.6 * mm});
            skSolve(sketch);
        }
        {
            var Q0;
            Q0 = qSketchRegion(id + "F3", true);
            var Q1;
            Q1=makeQuery(id+"F2.opChamfer","BLEND_FACE",FACE,{"disambiguationData":[OSD([sQuery(id+"F0.wireOp",EDGE,"E141")])]});
            extrude(context, id + "F4", {"entities" : qUnion([Q0, Q1]), "operationType" : NewBodyOperationType.REMOVE, "oppositeDirection" : true, "depth" : 1.6 * mm, "offsetDistance" : 25 * mm, "hasSecondDirection" : true, "secondDirectionOppositeDirection" : true, "secondDirectionDepth" : 0.9 * mm});
        }
    });
